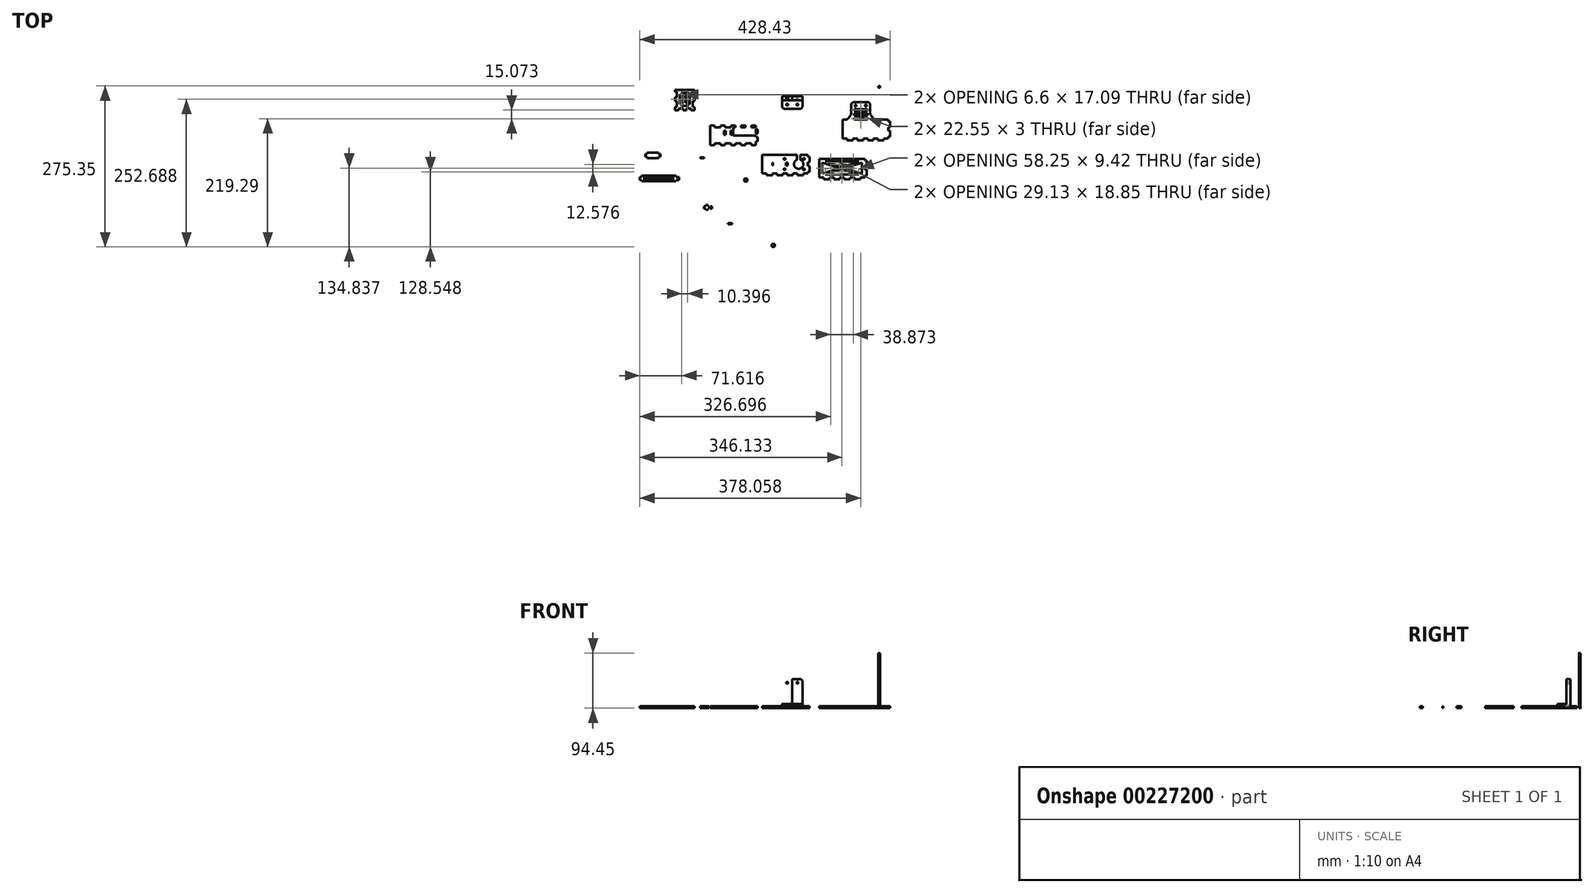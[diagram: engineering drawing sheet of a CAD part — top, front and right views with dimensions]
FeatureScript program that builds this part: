
annotation { "Feature Type Name" : "Feature", "Feature Type Description" : "" }
export const myFeature = defineFeature(function(context is Context, id is Id, definition is map)
    precondition{}
    {
        {
            var Q0;
            Q0=qCreatedBy(makeId("Top.planeOp"),FACE);
            var sketch = newSketch(context, id + "F0", { "sketchPlane" : qUnion([Q0])});
            skLineSegment(sketch, "E0.bottom", {"start": v(-53.14, -63.15) * mm, "end": v(-99.14, -63.15) * mm});
            skLineSegment(sketch, "E0.top", {"start": v(-53.14, -95.15) * mm, "end": v(-99.14, -95.15) * mm});
            skLineSegment(sketch, "E0.left", {"start": v(-53.14, -63.15) * mm, "end": v(-53.14, -95.15) * mm});
            skLineSegment(sketch, "E0.right", {"start": v(-99.14, -63.15) * mm, "end": v(-99.14, -95.15) * mm, "construction": true});
            skPoint(sketch, "E0.middle", {"position": v(-76.14, -79.15) * mm});
            skCircle(sketch, "E1", {"center": v(-58.64, -70.15) * mm, "radius": 1.5 * mm});
            skLineSegment(sketch, "E2.bottom", {"start": v(-141.01, -16.5) * mm, "end": v(-219.01, -16.5) * mm});
            skLineSegment(sketch, "E2.top", {"start": v(-141.01, -43.5) * mm, "end": v(-219.01, -43.5) * mm});
            skLineSegment(sketch, "E2.left", {"start": v(-141.01, -16.5) * mm, "end": v(-141.01, -43.5) * mm});
            skPoint(sketch, "E2.middle", {"position": v(-180.01, -30) * mm});
            skLineSegment(sketch, "E3", {"start": v(-99.14, -63.15) * mm, "end": v(-100.14, -63.15) * mm});
            skLineSegment(sketch, "E4", {"start": v(-100.14, -63.15) * mm, "end": v(-100.14, -95.15) * mm, "construction": true});
            skLineSegment(sketch, "E5", {"start": v(-100.14, -95.15) * mm, "end": v(-99.14, -95.15) * mm});
            skLineSegment(sketch, "E6.MirrorCS", {"start": v(-52.14, -63.15) * mm, "end": v(-52.14, -95.15) * mm});
            skLineSegment(sketch, "E7.MirrorCS", {"start": v(-53.14, -63.15) * mm, "end": v(-52.14, -63.15) * mm});
            skLineSegment(sketch, "E8.MirrorCS", {"start": v(-52.14, -95.15) * mm, "end": v(-53.14, -95.15) * mm});
            skLineSegment(sketch, "E9.MirrorCS", {"start": v(-52.14, -66.15) * mm, "end": v(-48.96, -66.15) * mm});
            skLineSegment(sketch, "E10.MirrorCS", {"start": v(-48.96, -66.15) * mm, "end": v(-48.96, -76.15) * mm});
            skLineSegment(sketch, "E11.MirrorCS", {"start": v(-48.96, -76.15) * mm, "end": v(-52.14, -76.15) * mm});
            skLineSegment(sketch, "E12.MirrorCS", {"start": v(-48.96, -82.15) * mm, "end": v(-52.14, -82.15) * mm});
            skLineSegment(sketch, "E13.MirrorCS", {"start": v(-48.96, -92.15) * mm, "end": v(-48.96, -82.15) * mm});
            skLineSegment(sketch, "E14.MirrorCS", {"start": v(-52.14, -92.15) * mm, "end": v(-48.96, -92.15) * mm});
            skCircle(sketch, "E15", {"center": v(-67.64, -79.15) * mm, "radius": 8 * mm});
            skLineSegment(sketch, "E16.bottom", {"start": v(-141.01, -19.5) * mm, "end": v(-137.84, -19.5) * mm});
            skLineSegment(sketch, "E16.top", {"start": v(-141.01, -27) * mm, "end": v(-137.84, -27) * mm});
            skLineSegment(sketch, "E16.left", {"start": v(-141.01, -19.5) * mm, "end": v(-141.01, -27) * mm});
            skLineSegment(sketch, "E16.right", {"start": v(-137.84, -19.5) * mm, "end": v(-137.84, -27) * mm});
            skLineSegment(sketch, "E17", {"start": v(-100.14, -63.15) * mm, "end": v(-130.14, -63.15) * mm});
            skLineSegment(sketch, "E18", {"start": v(-130.14, -63.15) * mm, "end": v(-130.14, -95.15) * mm});
            skLineSegment(sketch, "E19", {"start": v(-130.14, -95.15) * mm, "end": v(-100.14, -95.15) * mm});
            skLineSegment(sketch, "E20", {"start": v(-122.54, -95.15) * mm, "end": v(-122.54, -98.32) * mm});
            skLineSegment(sketch, "E21", {"start": v(-122.54, -98.32) * mm, "end": v(-112.54, -98.32) * mm});
            skLineSegment(sketch, "E22", {"start": v(-112.54, -98.32) * mm, "end": v(-112.54, -95.15) * mm});
            skLineSegment(sketch, "E23", {"start": v(-104.94, -95.15) * mm, "end": v(-104.94, -98.32) * mm});
            skLineSegment(sketch, "E24", {"start": v(-104.94, -98.32) * mm, "end": v(-94.94, -98.32) * mm});
            skLineSegment(sketch, "E25", {"start": v(-94.94, -98.32) * mm, "end": v(-94.94, -95.15) * mm});
            skLineSegment(sketch, "E26", {"start": v(-87.34, -95.15) * mm, "end": v(-87.34, -98.32) * mm});
            skLineSegment(sketch, "E27", {"start": v(-87.34, -98.32) * mm, "end": v(-77.34, -98.32) * mm});
            skLineSegment(sketch, "E28", {"start": v(-77.34, -98.32) * mm, "end": v(-77.34, -95.15) * mm});
            skLineSegment(sketch, "E29", {"start": v(-69.74, -95.15) * mm, "end": v(-69.74, -98.32) * mm});
            skLineSegment(sketch, "E30", {"start": v(-69.74, -98.32) * mm, "end": v(-59.74, -98.32) * mm});
            skLineSegment(sketch, "E31", {"start": v(-59.74, -98.32) * mm, "end": v(-59.74, -95.15) * mm});
            skLineSegment(sketch, "E32", {"start": v(-219.01, -43.5) * mm, "end": v(-219.01, -46.67) * mm});
            skLineSegment(sketch, "E33", {"start": v(-219.01, -46.67) * mm, "end": v(-211.41, -46.67) * mm});
            skLineSegment(sketch, "E34", {"start": v(-211.41, -46.67) * mm, "end": v(-211.41, -43.5) * mm});
            skLineSegment(sketch, "E35", {"start": v(-201.41, -43.5) * mm, "end": v(-201.41, -46.66) * mm});
            skLineSegment(sketch, "E36", {"start": v(-201.41, -46.66) * mm, "end": v(-193.81, -46.66) * mm});
            skLineSegment(sketch, "E37", {"start": v(-193.81, -46.66) * mm, "end": v(-193.81, -43.48) * mm});
            skLineSegment(sketch, "E38", {"start": v(-183.81, -43.5) * mm, "end": v(-183.81, -46.66) * mm});
            skLineSegment(sketch, "E39", {"start": v(-183.81, -46.66) * mm, "end": v(-176.21, -46.66) * mm});
            skLineSegment(sketch, "E40", {"start": v(-176.21, -46.66) * mm, "end": v(-176.21, -43.5) * mm});
            skLineSegment(sketch, "E41", {"start": v(-166.21, -43.5) * mm, "end": v(-166.21, -46.67) * mm});
            skLineSegment(sketch, "E42", {"start": v(-166.21, -46.67) * mm, "end": v(-158.61, -46.67) * mm});
            skLineSegment(sketch, "E43", {"start": v(-158.61, -46.67) * mm, "end": v(-158.61, -43.5) * mm});
            skLineSegment(sketch, "E44", {"start": v(-148.61, -43.5) * mm, "end": v(-148.61, -46.67) * mm});
            skLineSegment(sketch, "E45", {"start": v(-148.61, -46.67) * mm, "end": v(-141.01, -46.67) * mm});
            skLineSegment(sketch, "E46", {"start": v(-141.01, -46.67) * mm, "end": v(-141.01, -43.5) * mm});
            skLineSegment(sketch, "E47.MirrorCS", {"start": v(45.62, -69.95) * mm, "end": v(45.62, -101.95) * mm});
            skLineSegment(sketch, "E48.MirrorCS", {"start": v(44.62, -68.51) * mm, "end": v(45.62, -68.51) * mm});
            skLineSegment(sketch, "E49.MirrorCS", {"start": v(48.8, -72.95) * mm, "end": v(48.8, -82.95) * mm});
            skLineSegment(sketch, "E50.MirrorCS", {"start": v(48.8, -98.95) * mm, "end": v(48.8, -88.95) * mm});
            skLineSegment(sketch, "E51", {"start": v(-32.38, -69.95) * mm, "end": v(-32.38, -101.95) * mm});
            skLineSegment(sketch, "E52", {"start": v(-24.78, -101.95) * mm, "end": v(-24.78, -105.13) * mm});
            skLineSegment(sketch, "E53", {"start": v(-24.78, -105.13) * mm, "end": v(-14.78, -105.13) * mm});
            skLineSegment(sketch, "E54", {"start": v(-14.78, -105.13) * mm, "end": v(-14.78, -101.95) * mm});
            skLineSegment(sketch, "E55", {"start": v(-7.18, -101.95) * mm, "end": v(-7.18, -105.13) * mm});
            skLineSegment(sketch, "E56", {"start": v(-7.18, -105.13) * mm, "end": v(2.82, -105.13) * mm});
            skLineSegment(sketch, "E57", {"start": v(2.82, -105.13) * mm, "end": v(2.82, -101.95) * mm});
            skLineSegment(sketch, "E58", {"start": v(10.42, -101.95) * mm, "end": v(10.42, -105.13) * mm});
            skLineSegment(sketch, "E59", {"start": v(10.42, -105.13) * mm, "end": v(20.42, -105.13) * mm});
            skLineSegment(sketch, "E60", {"start": v(20.42, -105.13) * mm, "end": v(20.42, -101.95) * mm});
            skLineSegment(sketch, "E61", {"start": v(28.02, -101.95) * mm, "end": v(28.02, -105.13) * mm});
            skLineSegment(sketch, "E62", {"start": v(28.02, -105.13) * mm, "end": v(38.02, -105.13) * mm});
            skLineSegment(sketch, "E63", {"start": v(38.02, -105.13) * mm, "end": v(38.02, -101.95) * mm});
            skLineSegment(sketch, "E64.bottom", {"start": v(-249.2, 47.9) * mm, "end": v(-276.2, 47.9) * mm});
            skLineSegment(sketch, "E64.top", {"start": v(-249.2, 15.9) * mm, "end": v(-276.2, 15.9) * mm});
            skLineSegment(sketch, "E64.left", {"start": v(-249.2, 47.9) * mm, "end": v(-249.2, 15.9) * mm});
            skLineSegment(sketch, "E64.right", {"start": v(-276.2, 47.9) * mm, "end": v(-276.2, 15.9) * mm});
            skPoint(sketch, "E64.middle", {"position": v(-262.7, 31.9) * mm});
            skLineSegment(sketch, "E65", {"start": v(-262.7, 47.9) * mm, "end": v(-262.7, 15.9) * mm, "construction": true});
            skLineSegment(sketch, "E66", {"start": v(-265.7, 15.9) * mm, "end": v(-265.7, 12.72) * mm});
            skLineSegment(sketch, "E67", {"start": v(-265.7, 12.72) * mm, "end": v(-259.7, 12.72) * mm});
            skLineSegment(sketch, "E68", {"start": v(-259.7, 12.72) * mm, "end": v(-259.7, 15.9) * mm});
            skLineSegment(sketch, "E69", {"start": v(-252.2, 12.72) * mm, "end": v(-252.2, 15.9) * mm});
            skLineSegment(sketch, "E70", {"start": v(-249.2, 34.9) * mm, "end": v(-245.88, 34.9) * mm});
            skLineSegment(sketch, "E71", {"start": v(-245.88, 34.9) * mm, "end": v(-245.88, 28.9) * mm});
            skLineSegment(sketch, "E72", {"start": v(-245.88, 28.9) * mm, "end": v(-249.2, 28.9) * mm});
            skLineSegment(sketch, "E73", {"start": v(-249.2, 47.9) * mm, "end": v(-245.88, 47.9) * mm});
            skLineSegment(sketch, "E74", {"start": v(-245.88, 47.9) * mm, "end": v(-245.88, 44.9) * mm});
            skLineSegment(sketch, "E75", {"start": v(-245.88, 44.9) * mm, "end": v(-249.2, 44.9) * mm});
            skLineSegment(sketch, "E76", {"start": v(-276.2, 31.9) * mm, "end": v(-249.2, 31.9) * mm, "construction": true});
            skLineSegment(sketch, "E77.MirrorCS", {"start": v(-245.88, 18.9) * mm, "end": v(-249.2, 18.9) * mm});
            skLineSegment(sketch, "E78.MirrorCS", {"start": v(-245.88, 15.9) * mm, "end": v(-245.88, 18.9) * mm});
            skLineSegment(sketch, "E79.MirrorCS", {"start": v(-249.2, 15.9) * mm, "end": v(-245.88, 15.9) * mm});
            skLineSegment(sketch, "E80.MirrorCS", {"start": v(-276.2, 47.9) * mm, "end": v(-279.5, 47.9) * mm});
            skLineSegment(sketch, "E81.MirrorCS", {"start": v(-279.5, 44.9) * mm, "end": v(-276.2, 44.9) * mm});
            skLineSegment(sketch, "E82.MirrorCS", {"start": v(-279.5, 47.9) * mm, "end": v(-279.5, 44.9) * mm});
            skLineSegment(sketch, "E83.MirrorCS", {"start": v(-276.2, 34.9) * mm, "end": v(-279.5, 34.9) * mm});
            skLineSegment(sketch, "E84.MirrorCS", {"start": v(-279.5, 34.9) * mm, "end": v(-279.5, 28.9) * mm});
            skLineSegment(sketch, "E85.MirrorCS", {"start": v(-279.5, 28.9) * mm, "end": v(-276.2, 28.9) * mm});
            skLineSegment(sketch, "E86.MirrorCS", {"start": v(-279.5, 18.9) * mm, "end": v(-276.2, 18.9) * mm});
            skLineSegment(sketch, "E87.MirrorCS", {"start": v(-276.2, 15.9) * mm, "end": v(-279.5, 15.9) * mm});
            skLineSegment(sketch, "E88.MirrorCS", {"start": v(-279.5, 15.9) * mm, "end": v(-279.5, 18.9) * mm});
            skLineSegment(sketch, "E89", {"start": v(-252.2, 12.72) * mm, "end": v(-245.88, 12.72) * mm});
            skLineSegment(sketch, "E90", {"start": v(-245.88, 12.72) * mm, "end": v(-245.88, 15.9) * mm});
            skLineSegment(sketch, "E91.MirrorCS", {"start": v(-273.2, 12.72) * mm, "end": v(-273.2, 15.9) * mm});
            skLineSegment(sketch, "E92.MirrorCS", {"start": v(-273.2, 12.72) * mm, "end": v(-279.5, 12.72) * mm});
            skLineSegment(sketch, "E93.MirrorCS", {"start": v(-279.5, 12.72) * mm, "end": v(-279.5, 15.9) * mm});
            skLineSegment(sketch, "E94.bottom", {"start": v(-254.2, 42.9) * mm, "end": v(-271.2, 42.9) * mm});
            skLineSegment(sketch, "E94.top", {"start": v(-254.2, 20.9) * mm, "end": v(-271.2, 20.9) * mm});
            skLineSegment(sketch, "E94.left", {"start": v(-254.2, 42.9) * mm, "end": v(-254.2, 20.9) * mm});
            skLineSegment(sketch, "E94.right", {"start": v(-271.2, 42.9) * mm, "end": v(-271.2, 20.9) * mm});
            skLineSegment(sketch, "E95", {"start": v(-271.2, 42.9) * mm, "end": v(-254.2, 20.9) * mm, "construction": true});
            skLineSegment(sketch, "E96", {"start": v(-269.3, 42.9) * mm, "end": v(-254.2, 23.35) * mm});
            skLineSegment(sketch, "E97", {"start": v(-271.2, 40.44) * mm, "end": v(-256.1, 20.9) * mm});
            skLineSegment(sketch, "E98", {"start": v(-271.2, 20.9) * mm, "end": v(-254.2, 42.9) * mm, "construction": true});
            skLineSegment(sketch, "E99", {"start": v(-271.2, 23.35) * mm, "end": v(-256.1, 42.9) * mm});
            skLineSegment(sketch, "E100", {"start": v(-269.3, 20.9) * mm, "end": v(-254.2, 40.44) * mm});
            skLineSegment(sketch, "E101", {"start": v(-32.38, -85.95) * mm, "end": v(45.62, -85.95) * mm, "construction": true});
            skLineSegment(sketch, "E102.bottom", {"start": v(40.62, -74.95) * mm, "end": v(-27.38, -74.95) * mm});
            skLineSegment(sketch, "E102.top", {"start": v(40.62, -96.95) * mm, "end": v(-27.38, -96.95) * mm});
            skLineSegment(sketch, "E102.left", {"start": v(40.62, -74.95) * mm, "end": v(40.62, -96.95) * mm});
            skLineSegment(sketch, "E102.right", {"start": v(-27.38, -74.95) * mm, "end": v(-27.38, -96.95) * mm});
            skPoint(sketch, "E102.middle", {"position": v(6.62, -85.95) * mm});
            skLineSegment(sketch, "E103", {"start": v(-32.38, -69.95) * mm, "end": v(45.62, -69.95) * mm});
            skLineSegment(sketch, "E104", {"start": v(-32.38, -101.95) * mm, "end": v(45.62, -101.95) * mm});
            skLineSegment(sketch, "E105", {"start": v(48.8, -72.95) * mm, "end": v(45.62, -72.95) * mm});
            skLineSegment(sketch, "E106", {"start": v(48.8, -82.95) * mm, "end": v(45.62, -82.95) * mm});
            skLineSegment(sketch, "E107", {"start": v(48.8, -88.95) * mm, "end": v(45.62, -88.95) * mm});
            skLineSegment(sketch, "E108", {"start": v(48.8, -98.95) * mm, "end": v(45.62, -98.95) * mm});
            skLineSegment(sketch, "E109", {"start": v(-27.38, -74.95) * mm, "end": v(40.62, -96.95) * mm, "construction": true});
            skLineSegment(sketch, "E110", {"start": v(40.62, -74.95) * mm, "end": v(-27.38, -96.95) * mm, "construction": true});
            skLineSegment(sketch, "E111", {"start": v(-27.38, -76.53) * mm, "end": v(35.75, -96.95) * mm});
            skLineSegment(sketch, "E112", {"start": v(-22.5, -74.95) * mm, "end": v(40.62, -95.38) * mm});
            skLineSegment(sketch, "E113", {"start": v(-27.38, -95.38) * mm, "end": v(35.75, -74.95) * mm});
            skLineSegment(sketch, "E114", {"start": v(-22.5, -96.95) * mm, "end": v(40.62, -76.53) * mm});
            skCircle(sketch, "E115", {"center": v(-58.64, -70.15) * mm, "radius": 4 * mm, "construction": true});
            skCircle(sketch, "E116", {"center": v(-58.64, -88.05) * mm, "radius": 1.5 * mm});
            skCircle(sketch, "E117", {"center": v(-58.64, -88.05) * mm, "radius": 4 * mm, "construction": true});
            skLineSegment(sketch, "E118", {"start": v(-58.64, -66.15) * mm, "end": v(-58.64, -92.05) * mm, "construction": true});
            skCircle(sketch, "E119", {"center": v(-91.74, -70.15) * mm, "radius": 1.5 * mm});
            skCircle(sketch, "E120", {"center": v(-91.74, -70.15) * mm, "radius": 4 * mm, "construction": true});
            skLineSegment(sketch, "E121", {"start": v(-54.64, -70.15) * mm, "end": v(-95.74, -70.15) * mm, "construction": true});
            skCircle(sketch, "E122", {"center": v(-91.74, -88.05) * mm, "radius": 4 * mm, "construction": true});
            skCircle(sketch, "E123", {"center": v(-91.74, -88.05) * mm, "radius": 1.5 * mm});
            skLineSegment(sketch, "E124", {"start": v(-91.74, -66.15) * mm, "end": v(-91.74, -92.05) * mm, "construction": true});
            skLineSegment(sketch, "E125", {"start": v(-95.74, -88.05) * mm, "end": v(-54.64, -88.05) * mm, "construction": true});
            skCircle(sketch, "E126", {"center": v(-67.64, -79.15) * mm, "radius": 3 * mm});
            skLineSegment(sketch, "E127", {"start": v(-64.64, -79.15) * mm, "end": v(-64.64, -63.15) * mm});
            skLineSegment(sketch, "E128", {"start": v(-70.64, -79.15) * mm, "end": v(-70.64, -63.15) * mm});
            skLineSegment(sketch, "E129.bottom", {"start": v(-61.08, 30.24) * mm, "end": v(-96.08, 30.24) * mm});
            skLineSegment(sketch, "E129.top", {"start": v(-61.08, 15.24) * mm, "end": v(-96.08, 15.24) * mm});
            skLineSegment(sketch, "E129.left", {"start": v(-61.08, 30.24) * mm, "end": v(-61.08, 15.24) * mm});
            skLineSegment(sketch, "E129.right", {"start": v(-96.08, 30.24) * mm, "end": v(-96.08, 15.24) * mm});
            skPoint(sketch, "E129.middle", {"position": v(-78.58, 22.74) * mm});
            skLineSegment(sketch, "E130", {"start": v(-78.58, 30.24) * mm, "end": v(-78.58, 15.24) * mm});
            skCircle(sketch, "E131", {"center": v(-69.83, 22.74) * mm, "radius": 1.5 * mm});
            skCircle(sketch, "E132.MirrorC", {"center": v(-87.33, 22.74) * mm, "radius": 1.5 * mm});
            skLineSegment(sketch, "E133.right", {"start": v(-184.3, -29.24) * mm, "end": v(-184.3, -22.24) * mm});
            skPoint(sketch, "E133.middle", {"position": v(-199.51, -30) * mm});
            skLineSegment(sketch, "E134", {"start": v(-180.01, -30) * mm, "end": v(-219.01, -30) * mm});
            skLineSegment(sketch, "E135", {"start": v(-180.01, -30) * mm, "end": v(-141.01, -30) * mm});
            skLineSegment(sketch, "E136", {"start": v(-184.3, -29.24) * mm, "end": v(-181.13, -29.24) * mm});
            skLineSegment(sketch, "E137", {"start": v(-181.13, -29.24) * mm, "end": v(-181.13, -22.24) * mm});
            skLineSegment(sketch, "E138", {"start": v(-181.13, -22.24) * mm, "end": v(-184.3, -22.24) * mm});
            skLineSegment(sketch, "E139.MirrorCS", {"start": v(85.74, -3) * mm, "end": v(85.74, -35) * mm});
            skLineSegment(sketch, "E140.MirrorCS", {"start": v(89.63, 2.18) * mm, "end": v(90.63, 2.18) * mm});
            skLineSegment(sketch, "E141.MirrorCS", {"start": v(88.92, -6) * mm, "end": v(88.92, -16) * mm});
            skLineSegment(sketch, "E142.MirrorCS", {"start": v(88.92, -32) * mm, "end": v(88.92, -22) * mm});
            skLineSegment(sketch, "E143", {"start": v(7.74, -3) * mm, "end": v(7.74, -35) * mm});
            skLineSegment(sketch, "E144", {"start": v(15.34, -35) * mm, "end": v(15.34, -38.17) * mm});
            skLineSegment(sketch, "E145", {"start": v(15.34, -38.17) * mm, "end": v(25.34, -38.17) * mm});
            skLineSegment(sketch, "E146", {"start": v(25.34, -38.17) * mm, "end": v(25.34, -35) * mm});
            skLineSegment(sketch, "E147", {"start": v(32.94, -35) * mm, "end": v(32.94, -38.17) * mm});
            skLineSegment(sketch, "E148", {"start": v(32.94, -38.17) * mm, "end": v(42.94, -38.17) * mm});
            skLineSegment(sketch, "E149", {"start": v(42.94, -38.17) * mm, "end": v(42.94, -35) * mm});
            skLineSegment(sketch, "E150", {"start": v(50.54, -35) * mm, "end": v(50.54, -38.17) * mm});
            skLineSegment(sketch, "E151", {"start": v(50.54, -38.17) * mm, "end": v(60.54, -38.17) * mm});
            skLineSegment(sketch, "E152", {"start": v(60.54, -38.17) * mm, "end": v(60.54, -35) * mm});
            skLineSegment(sketch, "E153", {"start": v(68.14, -35) * mm, "end": v(68.14, -38.17) * mm});
            skLineSegment(sketch, "E154", {"start": v(68.14, -38.17) * mm, "end": v(78.14, -38.17) * mm});
            skLineSegment(sketch, "E155", {"start": v(78.14, -38.17) * mm, "end": v(78.14, -35) * mm});
            skPoint(sketch, "E156.middle", {"position": v(51.63, -13.82) * mm});
            skLineSegment(sketch, "E157", {"start": v(7.74, -3) * mm, "end": v(85.74, -3) * mm});
            skLineSegment(sketch, "E158", {"start": v(7.74, -35) * mm, "end": v(85.74, -35) * mm});
            skLineSegment(sketch, "E159", {"start": v(88.92, -6) * mm, "end": v(85.74, -6) * mm});
            skLineSegment(sketch, "E160", {"start": v(88.92, -16) * mm, "end": v(85.74, -16) * mm});
            skLineSegment(sketch, "E161", {"start": v(88.92, -22) * mm, "end": v(85.74, -22) * mm});
            skLineSegment(sketch, "E162", {"start": v(88.92, -32) * mm, "end": v(85.74, -32) * mm});
            skLineSegment(sketch, "E163.bottom", {"start": v(7.74, -35) * mm, "end": v(-10.26, -35) * mm});
            skLineSegment(sketch, "E163.top", {"start": v(7.74, -3) * mm, "end": v(-10.26, -3) * mm});
            skLineSegment(sketch, "E163.left", {"start": v(7.74, -35) * mm, "end": v(7.74, -3) * mm});
            skLineSegment(sketch, "E163.right", {"start": v(-10.26, -35) * mm, "end": v(-10.26, -3) * mm});
            skCircle(sketch, "E164", {"center": v(70.28, 53.06) * mm, "radius": 1.5 * mm});
            skLineSegment(sketch, "E165", {"start": v(-10.26, -25.65) * mm, "end": v(7.74, -25.65) * mm});
            skLineSegment(sketch, "E166", {"start": v(-10.26, -21.6) * mm, "end": v(7.74, -21.6) * mm});
            skLineSegment(sketch, "E167", {"start": v(7.74, -35) * mm, "end": v(-10.26, -21.6) * mm});
            skLineSegment(sketch, "E168", {"start": v(-160.5, -101.33) * mm, "end": v(-226.37, -69.2) * mm});
            skLineSegment(sketch, "E169", {"start": v(-226.37, -69.2) * mm, "end": v(-252.35, -69.2) * mm});
            skLineSegment(sketch, "E170", {"start": v(-160.5, -114) * mm, "end": v(-160.5, -101.33) * mm});
            skLineSegment(sketch, "E171", {"start": v(-252.35, -69.2) * mm, "end": v(-160.5, -114) * mm});
            skLineSegment(sketch, "E172", {"start": v(-160.5, -114) * mm, "end": v(-160.5, -69.2) * mm});
            skLineSegment(sketch, "E173", {"start": v(-160.5, -69.2) * mm, "end": v(-252.35, -69.2) * mm, "construction": true});
            skLineSegment(sketch, "E174.bottom", {"start": v(-160.5, -104.01) * mm, "end": v(-155.42, -104.01) * mm});
            skLineSegment(sketch, "E174.top", {"start": v(-160.5, -109.01) * mm, "end": v(-155.42, -109.01) * mm});
            skLineSegment(sketch, "E174.left", {"start": v(-160.5, -104.01) * mm, "end": v(-160.5, -109.01) * mm});
            skLineSegment(sketch, "E174.right", {"start": v(-155.42, -104.01) * mm, "end": v(-155.42, -109.01) * mm});
            skLineSegment(sketch, "E175", {"start": v(-249.28, -70.7) * mm, "end": v(-160.5, -70.7) * mm});
            skLineSegment(sketch, "E176", {"start": v(-160.5, -110.49) * mm, "end": v(-167.7, -110.49) * mm});
            skLineSegment(sketch, "E177", {"start": v(-160.5, -110.49) * mm, "end": v(-242.08, -70.7) * mm});
            skLineSegment(sketch, "E178.bottom", {"start": v(-236.19, -70.7) * mm, "end": v(-229.19, -70.7) * mm});
            skLineSegment(sketch, "E178.top", {"start": v(-236.19, -67.53) * mm, "end": v(-229.19, -67.53) * mm});
            skLineSegment(sketch, "E178.left", {"start": v(-236.19, -70.7) * mm, "end": v(-236.19, -67.53) * mm});
            skLineSegment(sketch, "E178.right", {"start": v(-229.19, -70.7) * mm, "end": v(-229.19, -67.53) * mm});
            skLineSegment(sketch, "E179", {"start": v(-87.33, 22.74) * mm, "end": v(-69.83, 22.74) * mm});
            skLineSegment(sketch, "E180.bottom", {"start": v(-192.13, -29.24) * mm, "end": v(-195.3, -29.24) * mm});
            skLineSegment(sketch, "E180.top", {"start": v(-192.13, -22.24) * mm, "end": v(-195.3, -22.24) * mm});
            skLineSegment(sketch, "E180.left", {"start": v(-192.13, -29.24) * mm, "end": v(-192.13, -22.24) * mm});
            skLineSegment(sketch, "E180.right", {"start": v(-195.3, -29.24) * mm, "end": v(-195.3, -22.24) * mm});
            skLineSegment(sketch, "E181", {"start": v(-193.71, -29.24) * mm, "end": v(-193.71, -22.24) * mm});
            skLineSegment(sketch, "E182", {"start": v(-182.71, -29.24) * mm, "end": v(-182.71, -22.24) * mm});
            skLineSegment(sketch, "E183", {"start": v(-219.01, -43.5) * mm, "end": v(-219.01, -16.5) * mm});
            skLineSegment(sketch, "E184", {"start": v(-180.01, -46.66) * mm, "end": v(-180.01, -9.6) * mm});
            skLineSegment(sketch, "E185.MirrorCS", {"start": v(-219.01, -13.32) * mm, "end": v(-211.41, -13.32) * mm});
            skLineSegment(sketch, "E186.MirrorCS", {"start": v(-219.01, -16.5) * mm, "end": v(-219.01, -13.32) * mm});
            skLineSegment(sketch, "E187.MirrorCS", {"start": v(-211.41, -13.32) * mm, "end": v(-211.41, -16.5) * mm});
            skLineSegment(sketch, "E188.MirrorCS", {"start": v(-201.41, -13.34) * mm, "end": v(-193.81, -13.34) * mm});
            skLineSegment(sketch, "E189.MirrorCS", {"start": v(-201.41, -16.5) * mm, "end": v(-201.41, -13.34) * mm});
            skLineSegment(sketch, "E190.MirrorCS", {"start": v(-193.81, -13.34) * mm, "end": v(-193.81, -16.51) * mm});
            skLineSegment(sketch, "E191.MirrorCS", {"start": v(-183.81, -13.34) * mm, "end": v(-176.21, -13.34) * mm});
            skLineSegment(sketch, "E192.MirrorCS", {"start": v(-183.81, -16.5) * mm, "end": v(-183.81, -13.34) * mm});
            skLineSegment(sketch, "E193.MirrorCS", {"start": v(-176.21, -13.34) * mm, "end": v(-176.21, -16.5) * mm});
            skLineSegment(sketch, "E194.MirrorCS", {"start": v(-166.21, -13.32) * mm, "end": v(-158.61, -13.32) * mm});
            skLineSegment(sketch, "E195.MirrorCS", {"start": v(-166.21, -16.5) * mm, "end": v(-166.21, -13.32) * mm});
            skLineSegment(sketch, "E196.MirrorCS", {"start": v(-158.61, -13.32) * mm, "end": v(-158.61, -16.5) * mm});
            skLineSegment(sketch, "E197.MirrorCS", {"start": v(-148.61, -16.5) * mm, "end": v(-148.61, -13.32) * mm});
            skLineSegment(sketch, "E198.MirrorCS", {"start": v(-148.61, -13.32) * mm, "end": v(-141.01, -13.32) * mm});
            skLineSegment(sketch, "E199.MirrorCS", {"start": v(-141.01, -13.32) * mm, "end": v(-141.01, -16.5) * mm});
            skLineSegment(sketch, "E200.MirrorCS", {"start": v(-141.01, -33) * mm, "end": v(-137.84, -33) * mm});
            skLineSegment(sketch, "E201.MirrorCS", {"start": v(-137.84, -40.5) * mm, "end": v(-137.84, -33) * mm});
            skLineSegment(sketch, "E202.MirrorCS", {"start": v(-141.01, -40.5) * mm, "end": v(-137.84, -40.5) * mm});
            skLineSegment(sketch, "E203.bottom", {"start": v(-108.6, -81.58) * mm, "end": v(-111.78, -81.58) * mm});
            skLineSegment(sketch, "E203.top", {"start": v(-108.6, -76.58) * mm, "end": v(-111.78, -76.58) * mm});
            skLineSegment(sketch, "E203.left", {"start": v(-108.6, -81.58) * mm, "end": v(-108.6, -76.58) * mm});
            skLineSegment(sketch, "E204", {"start": v(-111.78, -81.58) * mm, "end": v(-111.78, -76.58) * mm});
            skLineSegment(sketch, "E205.bottom", {"start": v(-121.6, 103.53) * mm, "end": v(-39.32, 103.53) * mm});
            skLineSegment(sketch, "E205.top", {"start": v(-121.6, 92.37) * mm, "end": v(-39.32, 92.37) * mm});
            skLineSegment(sketch, "E205.left", {"start": v(-121.6, 103.53) * mm, "end": v(-121.6, 92.37) * mm});
            skLineSegment(sketch, "E205.right", {"start": v(-39.32, 103.53) * mm, "end": v(-39.32, 92.37) * mm});
            skPoint(sketch, "E205.middle", {"position": v(-80.46, 97.95) * mm});
            skLineSegment(sketch, "E206", {"start": v(-80.46, 103.53) * mm, "end": v(-80.46, 92.37) * mm});
            skLineSegment(sketch, "E207", {"start": v(-113.85, -213.56) * mm, "end": v(-178.5, -182.02) * mm});
            skLineSegment(sketch, "E208", {"start": v(-178.5, -182.02) * mm, "end": v(-204.48, -182.02) * mm});
            skLineSegment(sketch, "E209", {"start": v(-113.85, -226.23) * mm, "end": v(-113.85, -213.56) * mm});
            skLineSegment(sketch, "E210", {"start": v(-204.48, -182.02) * mm, "end": v(-113.85, -226.23) * mm});
            skLineSegment(sketch, "E211", {"start": v(-113.85, -226.23) * mm, "end": v(-113.85, -182.02) * mm});
            skLineSegment(sketch, "E212", {"start": v(-113.85, -182.02) * mm, "end": v(-204.48, -182.02) * mm, "construction": true});
            skLineSegment(sketch, "E213.bottom", {"start": v(-113.85, -215.79) * mm, "end": v(-108.77, -215.79) * mm});
            skLineSegment(sketch, "E213.top", {"start": v(-113.85, -220.79) * mm, "end": v(-108.77, -220.79) * mm});
            skLineSegment(sketch, "E213.left", {"start": v(-113.85, -215.79) * mm, "end": v(-113.85, -220.79) * mm});
            skLineSegment(sketch, "E213.right", {"start": v(-108.77, -215.79) * mm, "end": v(-108.77, -220.79) * mm});
            skLineSegment(sketch, "E214", {"start": v(-201.41, -183.52) * mm, "end": v(-113.85, -183.52) * mm});
            skLineSegment(sketch, "E215", {"start": v(-113.85, -222.72) * mm, "end": v(-121.05, -222.72) * mm});
            skLineSegment(sketch, "E216", {"start": v(-113.85, -222.72) * mm, "end": v(-194.21, -183.52) * mm});
            skLineSegment(sketch, "E217.bottom", {"start": v(-188.33, -183.52) * mm, "end": v(-181.33, -183.52) * mm});
            skLineSegment(sketch, "E217.top", {"start": v(-188.33, -180.34) * mm, "end": v(-181.33, -180.34) * mm});
            skLineSegment(sketch, "E217.left", {"start": v(-188.33, -183.52) * mm, "end": v(-188.33, -180.34) * mm});
            skLineSegment(sketch, "E217.right", {"start": v(-181.33, -183.52) * mm, "end": v(-181.33, -180.34) * mm});
            skLineSegment(sketch, "E218.bottom", {"start": v(-219.33, -149.2) * mm, "end": v(-226.94, -149.2) * mm});
            skLineSegment(sketch, "E218.top", {"start": v(-219.33, -157.42) * mm, "end": v(-226.94, -157.42) * mm});
            skLineSegment(sketch, "E218.left", {"start": v(-219.33, -149.2) * mm, "end": v(-219.33, -157.42) * mm});
            skLineSegment(sketch, "E218.right", {"start": v(-226.94, -149.2) * mm, "end": v(-226.94, -157.42) * mm});
            skPoint(sketch, "E218.middle", {"position": v(-223.13, -153.3) * mm});
            skLineSegment(sketch, "E219.bottom", {"start": v(-219.33, -151.3) * mm, "end": v(-216.15, -151.3) * mm});
            skLineSegment(sketch, "E219.top", {"start": v(-219.33, -155.3) * mm, "end": v(-216.15, -155.3) * mm});
            skLineSegment(sketch, "E219.left", {"start": v(-219.33, -151.3) * mm, "end": v(-219.33, -155.3) * mm});
            skLineSegment(sketch, "E219.right", {"start": v(-216.15, -151.3) * mm, "end": v(-216.15, -155.3) * mm});
            skLineSegment(sketch, "E220", {"start": v(-223.13, -149.2) * mm, "end": v(-223.13, -157.42) * mm});
            skLineSegment(sketch, "E221.MirrorCS", {"start": v(-226.94, -151.3) * mm, "end": v(-230.12, -151.3) * mm});
            skLineSegment(sketch, "E222.MirrorCS", {"start": v(-230.12, -151.3) * mm, "end": v(-230.12, -155.3) * mm});
            skLineSegment(sketch, "E223.MirrorCS", {"start": v(-226.94, -155.3) * mm, "end": v(-230.12, -155.3) * mm});
            skLineSegment(sketch, "E224.bottom", {"start": v(-221.13, -151.3) * mm, "end": v(-225.13, -151.3) * mm});
            skLineSegment(sketch, "E224.top", {"start": v(-221.13, -155.3) * mm, "end": v(-225.13, -155.3) * mm});
            skLineSegment(sketch, "E224.left", {"start": v(-221.13, -151.3) * mm, "end": v(-221.13, -155.3) * mm});
            skLineSegment(sketch, "E224.right", {"start": v(-225.13, -151.3) * mm, "end": v(-225.13, -155.3) * mm});
            skLineSegment(sketch, "E225", {"start": v(-225.13, -151.3) * mm, "end": v(-221.13, -155.3) * mm});
            skLineSegment(sketch, "E226", {"start": v(-221.13, -151.3) * mm, "end": v(-225.13, -155.3) * mm});
            skLineSegment(sketch, "E227", {"start": v(-225.13, -152.01) * mm, "end": v(-221.84, -155.3) * mm});
            skLineSegment(sketch, "E228", {"start": v(-224.43, -151.3) * mm, "end": v(-221.13, -154.6) * mm});
            skLineSegment(sketch, "E229", {"start": v(-225.13, -154.6) * mm, "end": v(-221.84, -151.3) * mm});
            skLineSegment(sketch, "E230", {"start": v(-224.43, -155.3) * mm, "end": v(-221.13, -152.01) * mm});
            skLineSegment(sketch, "E231.bottom", {"start": v(-100.57, -76.58) * mm, "end": v(-97.4, -76.58) * mm});
            skLineSegment(sketch, "E231.top", {"start": v(-100.57, -81.58) * mm, "end": v(-97.4, -81.58) * mm});
            skLineSegment(sketch, "E231.left", {"start": v(-100.57, -76.58) * mm, "end": v(-100.57, -81.58) * mm});
            skLineSegment(sketch, "E231.right", {"start": v(-97.4, -76.58) * mm, "end": v(-97.4, -81.58) * mm});
            skLineSegment(sketch, "E232.bottom", {"start": v(-89.36, -76.58) * mm, "end": v(-86.18, -76.58) * mm});
            skLineSegment(sketch, "E232.top", {"start": v(-89.36, -81.58) * mm, "end": v(-86.18, -81.58) * mm});
            skLineSegment(sketch, "E232.left", {"start": v(-89.36, -76.58) * mm, "end": v(-89.36, -81.58) * mm});
            skLineSegment(sketch, "E232.right", {"start": v(-86.18, -76.58) * mm, "end": v(-86.18, -81.58) * mm});
            skLineSegment(sketch, "E233.bottom", {"start": v(54.82, 27.07) * mm, "end": v(22.27, 27.07) * mm});
            skLineSegment(sketch, "E233.top", {"start": v(54.82, 15.07) * mm, "end": v(22.27, 15.07) * mm});
            skLineSegment(sketch, "E233.left", {"start": v(54.82, 27.07) * mm, "end": v(54.82, 15.07) * mm});
            skLineSegment(sketch, "E233.right", {"start": v(22.27, 27.07) * mm, "end": v(22.27, 15.07) * mm});
            skPoint(sketch, "E233.middle", {"position": v(38.55, 21.07) * mm});
            skLineSegment(sketch, "E234", {"start": v(38.55, 15.07) * mm, "end": v(38.55, -3) * mm, "construction": true});
            skLineSegment(sketch, "E235", {"start": v(34.55, -3) * mm, "end": v(34.55, 15.07) * mm, "construction": true});
            skLineSegment(sketch, "E236.MirrorCS", {"start": v(42.55, -3) * mm, "end": v(42.55, 15.07) * mm, "construction": true});
            skCircle(sketch, "E237", {"center": v(47.3, 21.07) * mm, "radius": 1.5 * mm});
            skLineSegment(sketch, "E238", {"start": v(38.55, 21.07) * mm, "end": v(47.3, 21.07) * mm});
            skCircle(sketch, "E239.MirrorC", {"center": v(29.8, 21.07) * mm, "radius": 1.5 * mm});
            skLineSegment(sketch, "E240.MirrorCS", {"start": v(38.55, 21.07) * mm, "end": v(29.8, 21.07) * mm});
            skLineSegment(sketch, "E241", {"start": v(22.27, 15.07) * mm, "end": v(22.27, -3) * mm});
            skLineSegment(sketch, "E242", {"start": v(54.82, 15.07) * mm, "end": v(54.82, -3) * mm});
            skLineSegment(sketch, "E243", {"start": v(27.27, 15.07) * mm, "end": v(27.27, -3) * mm});
            skLineSegment(sketch, "E244.MirrorCS", {"start": v(49.82, 15.07) * mm, "end": v(49.82, -3) * mm});
            skLineSegment(sketch, "E245", {"start": v(27.27, 12.07) * mm, "end": v(49.82, 12.07) * mm});
            skLineSegment(sketch, "E246", {"start": v(27.27, 8.07) * mm, "end": v(49.82, 8.07) * mm});
            skLineSegment(sketch, "E247", {"start": v(27.27, 4) * mm, "end": v(49.82, 4) * mm});
            skLineSegment(sketch, "E248", {"start": v(27.27, 0) * mm, "end": v(49.82, 0) * mm});
            skLineSegment(sketch, "E249.bottom", {"start": v(-277.77, -99.12) * mm, "end": v(-336.33, -99.12) * mm});
            skLineSegment(sketch, "E249.top", {"start": v(-277.77, -108.12) * mm, "end": v(-336.33, -108.12) * mm});
            skLineSegment(sketch, "E249.left", {"start": v(-277.77, -99.12) * mm, "end": v(-277.77, -108.12) * mm});
            skLineSegment(sketch, "E249.right", {"start": v(-336.33, -99.12) * mm, "end": v(-336.33, -108.12) * mm});
            skPoint(sketch, "E249.middle", {"position": v(-307.05, -103.62) * mm});
            skLineSegment(sketch, "E250.bottom", {"start": v(-277.77, -101.12) * mm, "end": v(-272.7, -101.12) * mm});
            skLineSegment(sketch, "E250.top", {"start": v(-277.77, -106.12) * mm, "end": v(-272.7, -106.12) * mm});
            skLineSegment(sketch, "E250.left", {"start": v(-277.77, -101.12) * mm, "end": v(-277.77, -106.12) * mm});
            skLineSegment(sketch, "E250.right", {"start": v(-272.7, -101.12) * mm, "end": v(-272.7, -106.12) * mm});
            skLineSegment(sketch, "E251.bottom", {"start": v(-336.33, -101.12) * mm, "end": v(-339.5, -101.12) * mm});
            skLineSegment(sketch, "E251.top", {"start": v(-336.33, -106.12) * mm, "end": v(-339.5, -106.12) * mm});
            skLineSegment(sketch, "E251.left", {"start": v(-336.33, -101.12) * mm, "end": v(-336.33, -106.12) * mm});
            skLineSegment(sketch, "E251.right", {"start": v(-339.5, -101.12) * mm, "end": v(-339.5, -106.12) * mm});
            skPoint(sketch, "E252.oppositeSnap0", {"position": v(-110.2, -76.58) * mm});
            skLineSegment(sketch, "E252.bottom", {"start": v(-109.36, -81.58) * mm, "end": v(-112.53, -81.58) * mm});
            skLineSegment(sketch, "E252.top", {"start": v(-109.36, -76.58) * mm, "end": v(-112.53, -76.58) * mm});
            skLineSegment(sketch, "E252.left", {"start": v(-109.36, -81.58) * mm, "end": v(-109.36, -76.58) * mm});
            skLineSegment(sketch, "E252.right", {"start": v(-112.53, -81.58) * mm, "end": v(-112.53, -76.58) * mm});
            skLineSegment(sketch, "E253", {"start": v(-336.33, -103.62) * mm, "end": v(-277.77, -103.62) * mm});
            skLineSegment(sketch, "E254.bottom", {"start": v(-328.61, -101.12) * mm, "end": v(-331.79, -101.12) * mm});
            skLineSegment(sketch, "E254.top", {"start": v(-328.61, -106.12) * mm, "end": v(-331.79, -106.12) * mm});
            skLineSegment(sketch, "E254.left", {"start": v(-328.61, -101.12) * mm, "end": v(-328.61, -106.12) * mm});
            skLineSegment(sketch, "E254.right", {"start": v(-331.79, -101.12) * mm, "end": v(-331.79, -106.12) * mm});
            skPoint(sketch, "E254.middle", {"position": v(-330.2, -103.62) * mm});
            skLineSegment(sketch, "E255.bottom", {"start": v(-320.9, -101.12) * mm, "end": v(-324.07, -101.12) * mm});
            skLineSegment(sketch, "E255.top", {"start": v(-320.9, -106.12) * mm, "end": v(-324.07, -106.12) * mm});
            skLineSegment(sketch, "E255.left", {"start": v(-320.9, -101.12) * mm, "end": v(-320.9, -106.12) * mm});
            skLineSegment(sketch, "E255.right", {"start": v(-324.07, -101.12) * mm, "end": v(-324.07, -106.12) * mm});
            skPoint(sketch, "E255.middle", {"position": v(-322.48, -103.62) * mm});
            skLineSegment(sketch, "E256.bottom", {"start": v(-313.18, -101.12) * mm, "end": v(-316.35, -101.12) * mm});
            skLineSegment(sketch, "E256.top", {"start": v(-313.18, -106.12) * mm, "end": v(-316.35, -106.12) * mm});
            skLineSegment(sketch, "E256.left", {"start": v(-313.18, -101.12) * mm, "end": v(-313.18, -106.12) * mm});
            skLineSegment(sketch, "E256.right", {"start": v(-316.35, -101.12) * mm, "end": v(-316.35, -106.12) * mm});
            skPoint(sketch, "E256.middle", {"position": v(-314.77, -103.62) * mm});
            skLineSegment(sketch, "E257.bottom", {"start": v(-305.46, -101.12) * mm, "end": v(-308.64, -101.12) * mm});
            skLineSegment(sketch, "E257.top", {"start": v(-305.46, -106.12) * mm, "end": v(-308.64, -106.12) * mm});
            skLineSegment(sketch, "E257.left", {"start": v(-305.46, -101.12) * mm, "end": v(-305.46, -106.12) * mm});
            skLineSegment(sketch, "E257.right", {"start": v(-308.64, -101.12) * mm, "end": v(-308.64, -106.12) * mm});
            skLineSegment(sketch, "E258.bottom", {"start": v(-297.75, -101.12) * mm, "end": v(-300.92, -101.12) * mm});
            skLineSegment(sketch, "E258.top", {"start": v(-297.75, -106.12) * mm, "end": v(-300.92, -106.12) * mm});
            skLineSegment(sketch, "E258.left", {"start": v(-297.75, -101.12) * mm, "end": v(-297.75, -106.12) * mm});
            skLineSegment(sketch, "E258.right", {"start": v(-300.92, -101.12) * mm, "end": v(-300.92, -106.12) * mm});
            skPoint(sketch, "E258.middle", {"position": v(-299.33, -103.62) * mm});
            skLineSegment(sketch, "E259.bottom", {"start": v(-290.03, -101.18) * mm, "end": v(-293.2, -101.18) * mm});
            skLineSegment(sketch, "E259.top", {"start": v(-290.03, -106.18) * mm, "end": v(-293.2, -106.18) * mm});
            skLineSegment(sketch, "E259.left", {"start": v(-290.03, -101.18) * mm, "end": v(-290.03, -106.18) * mm});
            skLineSegment(sketch, "E259.right", {"start": v(-293.2, -101.18) * mm, "end": v(-293.2, -106.18) * mm});
            skPoint(sketch, "E259.middle", {"position": v(-291.62, -103.68) * mm});
            skLineSegment(sketch, "E260.bottom", {"start": v(-282.31, -101.31) * mm, "end": v(-285.49, -101.31) * mm});
            skLineSegment(sketch, "E260.top", {"start": v(-282.31, -106.31) * mm, "end": v(-285.49, -106.31) * mm});
            skLineSegment(sketch, "E260.left", {"start": v(-282.31, -101.31) * mm, "end": v(-282.31, -106.31) * mm});
            skLineSegment(sketch, "E260.right", {"start": v(-285.49, -101.31) * mm, "end": v(-285.49, -106.31) * mm});
            skPoint(sketch, "E260.middle", {"position": v(-283.9, -103.81) * mm});
            skLineSegment(sketch, "E261.bottom", {"start": v(-307.28, -59.68) * mm, "end": v(-327.28, -59.68) * mm});
            skLineSegment(sketch, "E261.top", {"start": v(-307.28, -68.68) * mm, "end": v(-327.28, -68.68) * mm});
            skLineSegment(sketch, "E261.left", {"start": v(-307.28, -59.68) * mm, "end": v(-307.28, -68.68) * mm});
            skLineSegment(sketch, "E261.right", {"start": v(-327.28, -59.68) * mm, "end": v(-327.28, -68.68) * mm});
            skPoint(sketch, "E261.middle", {"position": v(-317.28, -64.18) * mm});
            skLineSegment(sketch, "E262", {"start": v(-307.28, -64.18) * mm, "end": v(-304.1, -64.18) * mm});
            skPoint(sketch, "E262.endSnap0", {"position": v(-307.28, -64.18) * mm});
            skLineSegment(sketch, "E263", {"start": v(-304.1, -64.18) * mm, "end": v(-304.1, -61.68) * mm});
            skLineSegment(sketch, "E264", {"start": v(-304.1, -61.68) * mm, "end": v(-307.28, -61.68) * mm});
            skLineSegment(sketch, "E265.MirrorCS", {"start": v(-304.1, -66.68) * mm, "end": v(-307.28, -66.68) * mm});
            skLineSegment(sketch, "E266.MirrorCS", {"start": v(-304.1, -64.18) * mm, "end": v(-304.1, -66.68) * mm});
            skLineSegment(sketch, "E267", {"start": v(-317.28, -68.68) * mm, "end": v(-317.28, -59.68) * mm});
            skLineSegment(sketch, "E268.MirrorCS", {"start": v(-330.46, -61.68) * mm, "end": v(-327.28, -61.68) * mm});
            skLineSegment(sketch, "E269.MirrorCS", {"start": v(-330.46, -64.18) * mm, "end": v(-330.46, -61.68) * mm});
            skLineSegment(sketch, "E270.MirrorCS", {"start": v(-330.46, -64.18) * mm, "end": v(-330.46, -66.68) * mm});
            skLineSegment(sketch, "E271.MirrorCS", {"start": v(-330.46, -66.68) * mm, "end": v(-327.28, -66.68) * mm});
            skLineSegment(sketch, "E272.MirrorCS", {"start": v(-327.28, -64.18) * mm, "end": v(-330.46, -64.18) * mm});
            skPoint(sketch, "E273", {"position": v(-223.3, -70.7) * mm});
            skPoint(sketch, "E274", {"position": v(-175.44, -183.52) * mm});
            skLineSegment(sketch, "E275", {"start": v(-184.83, -183.52) * mm, "end": v(-113.85, -218.14) * mm});
            skLineSegment(sketch, "E276", {"start": v(-175.77, -190.16) * mm, "end": v(-174.02, -186.57) * mm});
            skLineSegment(sketch, "E277", {"start": v(-174.02, -186.57) * mm, "end": v(-171.17, -187.96) * mm});
            skLineSegment(sketch, "E278", {"start": v(-171.17, -187.96) * mm, "end": v(-172.92, -191.55) * mm});
            skLineSegment(sketch, "E279", {"start": v(-172.92, -191.55) * mm, "end": v(-175.77, -190.16) * mm});
            skLineSegment(sketch, "E280", {"start": v(-168.5, -193.71) * mm, "end": v(-166.74, -190.12) * mm});
            skLineSegment(sketch, "E281", {"start": v(-166.74, -190.12) * mm, "end": v(-163.88, -191.5) * mm});
            skLineSegment(sketch, "E282", {"start": v(-163.88, -191.5) * mm, "end": v(-165.64, -195.1) * mm});
            skLineSegment(sketch, "E283", {"start": v(-165.64, -195.1) * mm, "end": v(-168.5, -193.71) * mm});
            skLineSegment(sketch, "E284", {"start": v(-159.46, -193.67) * mm, "end": v(-161.21, -197.26) * mm});
            skLineSegment(sketch, "E285", {"start": v(-161.21, -197.26) * mm, "end": v(-158.36, -198.65) * mm});
            skLineSegment(sketch, "E286", {"start": v(-158.36, -198.65) * mm, "end": v(-156.6, -195.06) * mm});
            skLineSegment(sketch, "E287", {"start": v(-156.6, -195.06) * mm, "end": v(-159.46, -193.67) * mm});
            skLineSegment(sketch, "E288", {"start": v(-152.09, -197.26) * mm, "end": v(-153.84, -200.86) * mm});
            skLineSegment(sketch, "E289", {"start": v(-153.84, -200.86) * mm, "end": v(-150.99, -202.25) * mm});
            skLineSegment(sketch, "E290", {"start": v(-150.99, -202.25) * mm, "end": v(-149.23, -198.65) * mm});
            skLineSegment(sketch, "E291", {"start": v(-149.23, -198.65) * mm, "end": v(-152.09, -197.26) * mm});
            skLineSegment(sketch, "E292", {"start": v(-143.64, -201.12) * mm, "end": v(-145.4, -204.71) * mm});
            skLineSegment(sketch, "E293", {"start": v(-145.4, -204.71) * mm, "end": v(-142.54, -206.1) * mm});
            skLineSegment(sketch, "E294", {"start": v(-142.54, -206.1) * mm, "end": v(-140.79, -202.5) * mm});
            skLineSegment(sketch, "E295", {"start": v(-140.79, -202.5) * mm, "end": v(-143.64, -201.12) * mm});
            skLineSegment(sketch, "E296", {"start": v(-138.25, -208.46) * mm, "end": v(-136.5, -204.86) * mm});
            skLineSegment(sketch, "E297", {"start": v(-136.5, -204.86) * mm, "end": v(-133.42, -206.36) * mm});
            skLineSegment(sketch, "E298", {"start": v(-133.42, -206.36) * mm, "end": v(-135.18, -209.96) * mm});
            skLineSegment(sketch, "E299", {"start": v(-135.18, -209.96) * mm, "end": v(-138.25, -208.46) * mm});
            skLineSegment(sketch, "E300", {"start": v(-130.18, -212.4) * mm, "end": v(-128.43, -208.8) * mm});
            skLineSegment(sketch, "E301", {"start": v(-128.43, -208.8) * mm, "end": v(-125.58, -210.2) * mm});
            skLineSegment(sketch, "E302", {"start": v(-125.58, -210.2) * mm, "end": v(-127.33, -213.79) * mm});
            skLineSegment(sketch, "E303", {"start": v(-127.33, -213.79) * mm, "end": v(-130.18, -212.4) * mm});
            skLineSegment(sketch, "E304.bottom", {"start": v(80.74, -8) * mm, "end": v(12.74, -8) * mm});
            skLineSegment(sketch, "E304.top", {"start": v(80.74, -30) * mm, "end": v(12.74, -30) * mm});
            skLineSegment(sketch, "E304.left", {"start": v(80.74, -8) * mm, "end": v(80.74, -30) * mm});
            skLineSegment(sketch, "E304.right", {"start": v(12.74, -8) * mm, "end": v(12.74, -30) * mm});
            skPoint(sketch, "E304.middle", {"position": v(46.74, -19) * mm});
            skPoint(sketch, "E304.middle.positionSnap0", {"position": v(46.74, -3) * mm});
            skPoint(sketch, "E304.middle.positionSnap1", {"position": v(7.74, -19) * mm});
            skPoint(sketch, "E304.centerSnap0", {"position": v(46.74, -3) * mm});
            skPoint(sketch, "E304.centerSnap1", {"position": v(7.74, -19) * mm});
            skLineSegment(sketch, "E305", {"start": v(12.74, -8) * mm, "end": v(80.74, -30) * mm, "construction": true});
            skLineSegment(sketch, "E306", {"start": v(80.74, -8) * mm, "end": v(12.74, -30) * mm, "construction": true});
            skLineSegment(sketch, "E307", {"start": v(12.74, -28.42) * mm, "end": v(75.87, -8) * mm});
            skLineSegment(sketch, "E308", {"start": v(17.61, -30) * mm, "end": v(80.74, -9.58) * mm});
            skLineSegment(sketch, "E309", {"start": v(12.74, -9.58) * mm, "end": v(75.87, -30) * mm});
            skLineSegment(sketch, "E310", {"start": v(17.61, -8) * mm, "end": v(80.74, -28.42) * mm});
            skLineSegment(sketch, "E311", {"start": v(15.42, -3) * mm, "end": v(22.27, 6.04) * mm});
            skLineSegment(sketch, "E312.MirrorCS", {"start": v(61.68, -3) * mm, "end": v(54.82, 6.04) * mm});
            skSolve(sketch);
        }
        {
            var Q0;
            {var subQ0=sQuery(id+"F0.wireOp",EDGE,"E229");var subQ3=sQuery(id+"F0.wireOp",EDGE,"E225");var subQ5=makeQuery(id+"F0.imprint","INTERSECT",VERTEX,{"derivedFrom":[subQ3,subQ0]});Q0=makeQuery(id+"F0.imprint","IMPRINT",FACE,{"disambiguationData":[TD([[makeQuery(id+"F0.imprint","IMPRINT",EDGE,{"disambiguationData":[TD([[subQ5,-1.0]])],"derivedFrom":subQ3}),1.0]])]});}
            var Q1;
            {var subQ0=sQuery(id+"F0.wireOp",EDGE,"E70");Q1=makeQuery(id+"F0.imprint","IMPRINT",FACE,{"disambiguationData":[TD([[makeQuery(id+"F0.imprint","IMPRINT",EDGE,{"derivedFrom":subQ0}),-1.0]])]});}
            var Q2;
            {var subQ16=sQuery(id+"F0.wireOp",EDGE,"E64.bottom");Q2=makeQuery(id+"F0.imprint","IMPRINT",FACE,{"disambiguationData":[TD([[makeQuery(id+"F0.imprint","IMPRINT",EDGE,{"derivedFrom":subQ16}),1.0]])]});}
            var Q3;
            {var subQ5=sQuery(id+"F0.wireOp",EDGE,"E94.left");var subQ6=sQuery(id+"F0.wireOp",EDGE,"E94.bottom");var subQ7=makeQuery(id+"F0.imprint","INTERSECT",VERTEX,{"derivedFrom":[subQ6,subQ5]});Q3=makeQuery(id+"F0.imprint","IMPRINT",FACE,{"disambiguationData":[TD([[makeQuery(id+"F0.imprint","IMPRINT",EDGE,{"disambiguationData":[TD([[subQ7,-1.0]])],"derivedFrom":subQ6}),1.0]])]});}
            var Q4;
            {var subQ1=sQuery(id+"F0.wireOp",EDGE,"E69");Q4=makeQuery(id+"F0.imprint","IMPRINT",FACE,{"disambiguationData":[TD([[makeQuery(id+"F0.imprint","IMPRINT",EDGE,{"derivedFrom":subQ1}),-1.0]])]});}
            var Q5;
            {var subQ0=sQuery(id+"F0.wireOp",EDGE,"E80.MirrorCS");Q5=makeQuery(id+"F0.imprint","IMPRINT",FACE,{"disambiguationData":[TD([[makeQuery(id+"F0.imprint","IMPRINT",EDGE,{"derivedFrom":subQ0}),1.0]])]});}
            var Q6;
            {var subQ1=sQuery(id+"F0.wireOp",EDGE,"E94.right");var subQ5=sQuery(id+"F0.wireOp",EDGE,"E94.bottom");var subQ6=makeQuery(id+"F0.imprint","INTERSECT",VERTEX,{"derivedFrom":[subQ5,subQ1]});Q6=makeQuery(id+"F0.imprint","IMPRINT",FACE,{"disambiguationData":[TD([[makeQuery(id+"F0.imprint","IMPRINT",EDGE,{"disambiguationData":[TD([[subQ6,1.0]])],"derivedFrom":subQ5}),1.0]])]});}
            var Q7;
            {var subQ0=sQuery(id+"F0.wireOp",EDGE,"E83.MirrorCS");Q7=makeQuery(id+"F0.imprint","IMPRINT",FACE,{"disambiguationData":[TD([[makeQuery(id+"F0.imprint","IMPRINT",EDGE,{"derivedFrom":subQ0}),1.0]])]});}
            var Q8;
            {var subQ2=sQuery(id+"F0.wireOp",EDGE,"E77.MirrorCS");Q8=makeQuery(id+"F0.imprint","IMPRINT",FACE,{"disambiguationData":[TD([[makeQuery(id+"F0.imprint","IMPRINT",EDGE,{"derivedFrom":subQ2}),1.0]])]});}
            var Q9;
            {var subQ1=sQuery(id+"F0.wireOp",EDGE,"E94.right");var subQ7=sQuery(id+"F0.wireOp",EDGE,"E94.top");var subQ8=makeQuery(id+"F0.imprint","INTERSECT",VERTEX,{"derivedFrom":[subQ7,subQ1]});Q9=makeQuery(id+"F0.imprint","IMPRINT",FACE,{"disambiguationData":[TD([[makeQuery(id+"F0.imprint","IMPRINT",EDGE,{"disambiguationData":[TD([[subQ8,1.0]])],"derivedFrom":subQ7}),-1.0]])]});}
            var Q10;
            {var subQ2=sQuery(id+"F0.wireOp",EDGE,"E86.MirrorCS");Q10=makeQuery(id+"F0.imprint","IMPRINT",FACE,{"disambiguationData":[TD([[makeQuery(id+"F0.imprint","IMPRINT",EDGE,{"derivedFrom":subQ2}),-1.0]])]});}
            var Q11;
            {var subQ0=sQuery(id+"F0.wireOp",EDGE,"E66");Q11=makeQuery(id+"F0.imprint","IMPRINT",FACE,{"disambiguationData":[TD([[makeQuery(id+"F0.imprint","IMPRINT",EDGE,{"derivedFrom":subQ0}),1.0]])]});}
            var Q12;
            {var subQ0=sQuery(id+"F0.wireOp",EDGE,"E73");Q12=makeQuery(id+"F0.imprint","IMPRINT",FACE,{"disambiguationData":[TD([[makeQuery(id+"F0.imprint","IMPRINT",EDGE,{"derivedFrom":subQ0}),-1.0]])]});}
            var Q13;
            {var subQ0=sQuery(id+"F0.wireOp",EDGE,"E99");var subQ1=sQuery(id+"F0.wireOp",EDGE,"E96");var subQ2=makeQuery(id+"F0.imprint","INTERSECT",VERTEX,{"derivedFrom":[subQ1,subQ0]});Q13=makeQuery(id+"F0.imprint","IMPRINT",FACE,{"disambiguationData":[TD([[makeQuery(id+"F0.imprint","IMPRINT",EDGE,{"disambiguationData":[TD([[subQ2,-1.0]])],"derivedFrom":subQ1}),-1.0]])]});}
            var Q14;
            {var subQ8=sQuery(id+"F0.wireOp",EDGE,"E16.left");Q14=makeQuery(id+"F0.imprint","IMPRINT",FACE,{"disambiguationData":[TD([[makeQuery(id+"F0.imprint","IMPRINT",EDGE,{"derivedFrom":subQ8}),-1.0]])]});}
            var Q15;
            {var subQ8=sQuery(id+"F0.wireOp",EDGE,"E16.left");Q15=makeQuery(id+"F0.imprint","IMPRINT",FACE,{"disambiguationData":[TD([[makeQuery(id+"F0.imprint","IMPRINT",EDGE,{"derivedFrom":subQ8}),-1.0]])]});}
            var Q16;
            {var subQ9=sQuery(id+"F0.wireOp",EDGE,"E135");Q16=makeQuery(id+"F0.imprint","IMPRINT",FACE,{"disambiguationData":[TD([[makeQuery(id+"F0.imprint","IMPRINT",EDGE,{"derivedFrom":subQ9}),-1.0]])]});}
            var Q17;
            {var subQ9=sQuery(id+"F0.wireOp",EDGE,"E135");Q17=makeQuery(id+"F0.imprint","IMPRINT",FACE,{"disambiguationData":[TD([[makeQuery(id+"F0.imprint","IMPRINT",EDGE,{"derivedFrom":subQ9}),-1.0]])]});}
            var Q18;
            {var subQ2=sQuery(id+"F0.wireOp",EDGE,"E44");Q18=makeQuery(id+"F0.imprint","IMPRINT",FACE,{"disambiguationData":[TD([[makeQuery(id+"F0.imprint","IMPRINT",EDGE,{"derivedFrom":subQ2}),1.0]])]});}
            var Q19;
            {var subQ0=sQuery(id+"F0.wireOp",EDGE,"E41");Q19=makeQuery(id+"F0.imprint","IMPRINT",FACE,{"disambiguationData":[TD([[makeQuery(id+"F0.imprint","IMPRINT",EDGE,{"derivedFrom":subQ0}),1.0]])]});}
            var Q20;
            {var subQ0=sQuery(id+"F0.wireOp",EDGE,"E35");Q20=makeQuery(id+"F0.imprint","IMPRINT",FACE,{"disambiguationData":[TD([[makeQuery(id+"F0.imprint","IMPRINT",EDGE,{"derivedFrom":subQ0}),1.0]])]});}
            var Q21;
            {var subQ0=sQuery(id+"F0.wireOp",EDGE,"E32");Q21=makeQuery(id+"F0.imprint","IMPRINT",FACE,{"disambiguationData":[TD([[makeQuery(id+"F0.imprint","IMPRINT",EDGE,{"derivedFrom":subQ0}),1.0]])]});}
            var Q22;
            {var subQ0=sQuery(id+"F0.wireOp",EDGE,"E38");Q22=makeQuery(id+"F0.imprint","IMPRINT",FACE,{"disambiguationData":[TD([[makeQuery(id+"F0.imprint","IMPRINT",EDGE,{"derivedFrom":subQ0}),1.0]])]});}
            var Q23;
            Q23=makeQuery(id+"F0.imprint","IMPRINT",FACE,{"disambiguationData":[TD([[makeQuery(id+"F0.imprint","IMPRINT",EDGE,{"derivedFrom":sQuery(id+"F0.wireOp",EDGE,"E16.bottom")}),-1.0]])]});
            var Q24;
            {var subQ1=sQuery(id+"F0.wireOp",EDGE,"E4");Q24=makeQuery(id+"F0.imprint","IMPRINT",FACE,{"disambiguationData":[TD([[makeQuery(id+"F0.imprint","IMPRINT",EDGE,{"derivedFrom":subQ1}),-1.0]])]});}
            var Q25;
            {var subQ0=sQuery(id+"F0.wireOp",EDGE,"E12.MirrorCS");Q25=makeQuery(id+"F0.imprint","IMPRINT",FACE,{"disambiguationData":[TD([[makeQuery(id+"F0.imprint","IMPRINT",EDGE,{"derivedFrom":subQ0}),1.0]])]});}
            var Q26;
            {var subQ0=sQuery(id+"F0.wireOp",EDGE,"E9.MirrorCS");Q26=makeQuery(id+"F0.imprint","IMPRINT",FACE,{"disambiguationData":[TD([[makeQuery(id+"F0.imprint","IMPRINT",EDGE,{"derivedFrom":subQ0}),-1.0]])]});}
            var Q27;
            {var subQ0=sQuery(id+"F0.wireOp",EDGE,"E29");Q27=makeQuery(id+"F0.imprint","IMPRINT",FACE,{"disambiguationData":[TD([[makeQuery(id+"F0.imprint","IMPRINT",EDGE,{"derivedFrom":subQ0}),1.0]])]});}
            var Q28;
            {var subQ0=sQuery(id+"F0.wireOp",EDGE,"E26");Q28=makeQuery(id+"F0.imprint","IMPRINT",FACE,{"disambiguationData":[TD([[makeQuery(id+"F0.imprint","IMPRINT",EDGE,{"derivedFrom":subQ0}),1.0]])]});}
            var Q29;
            {var subQ0=sQuery(id+"F0.wireOp",EDGE,"E20");Q29=makeQuery(id+"F0.imprint","IMPRINT",FACE,{"disambiguationData":[TD([[makeQuery(id+"F0.imprint","IMPRINT",EDGE,{"derivedFrom":subQ0}),1.0]])]});}
            var Q30;
            {var subQ1=sQuery(id+"F0.wireOp",EDGE,"E5");Q30=makeQuery(id+"F0.imprint","IMPRINT",FACE,{"disambiguationData":[TD([[makeQuery(id+"F0.imprint","IMPRINT",EDGE,{"derivedFrom":subQ1}),-1.0]])]});}
            var Q31;
            Q31=makeQuery(id+"F0.imprint","IMPRINT",FACE,{"disambiguationData":[TD([[makeQuery(id+"F0.imprint","IMPRINT",EDGE,{"derivedFrom":sQuery(id+"F0.wireOp",EDGE,"E0.right")}),-1.0]])]});
            var Q32;
            {var subQ1=sQuery(id+"F0.wireOp",EDGE,"E0.left");Q32=makeQuery(id+"F0.imprint","IMPRINT",FACE,{"disambiguationData":[TD([[makeQuery(id+"F0.imprint","IMPRINT",EDGE,{"derivedFrom":subQ1}),-1.0]])]});}
            var Q33;
            {var subQ3=sQuery(id+"F0.wireOp",EDGE,"E51");Q33=makeQuery(id+"F0.imprint","IMPRINT",FACE,{"disambiguationData":[TD([[makeQuery(id+"F0.imprint","IMPRINT",EDGE,{"derivedFrom":subQ3}),1.0]])]});}
            var Q34;
            {var subQ0=sQuery(id+"F0.wireOp",EDGE,"E52");Q34=makeQuery(id+"F0.imprint","IMPRINT",FACE,{"disambiguationData":[TD([[makeQuery(id+"F0.imprint","IMPRINT",EDGE,{"derivedFrom":subQ0}),1.0]])]});}
            var Q35;
            {var subQ0=sQuery(id+"F0.wireOp",EDGE,"E58");Q35=makeQuery(id+"F0.imprint","IMPRINT",FACE,{"disambiguationData":[TD([[makeQuery(id+"F0.imprint","IMPRINT",EDGE,{"derivedFrom":subQ0}),1.0]])]});}
            var Q36;
            {var subQ0=sQuery(id+"F0.wireOp",EDGE,"E61");Q36=makeQuery(id+"F0.imprint","IMPRINT",FACE,{"disambiguationData":[TD([[makeQuery(id+"F0.imprint","IMPRINT",EDGE,{"derivedFrom":subQ0}),1.0]])]});}
            var Q37;
            Q37=makeQuery(id+"F0.imprint","IMPRINT",FACE,{"disambiguationData":[TD([[makeQuery(id+"F0.imprint","IMPRINT",EDGE,{"derivedFrom":sQuery(id+"F0.wireOp",EDGE,"E49.MirrorCS")}),-1.0]])]});
            var Q38;
            {var subQ1=sQuery(id+"F0.wireOp",EDGE,"E102.left");var subQ6=sQuery(id+"F0.wireOp",EDGE,"E102.top");var subQ9=makeQuery(id+"F0.imprint","INTERSECT",VERTEX,{"derivedFrom":[subQ6,subQ1]});Q38=makeQuery(id+"F0.imprint","IMPRINT",FACE,{"disambiguationData":[TD([[makeQuery(id+"F0.imprint","IMPRINT",EDGE,{"disambiguationData":[TD([[subQ9,-1.0]])],"derivedFrom":subQ6}),-1.0]])]});}
            var Q39;
            {var subQ1=sQuery(id+"F0.wireOp",EDGE,"E102.right");var subQ5=sQuery(id+"F0.wireOp",EDGE,"E102.top");var subQ6=makeQuery(id+"F0.imprint","INTERSECT",VERTEX,{"derivedFrom":[subQ5,subQ1]});Q39=makeQuery(id+"F0.imprint","IMPRINT",FACE,{"disambiguationData":[TD([[makeQuery(id+"F0.imprint","IMPRINT",EDGE,{"disambiguationData":[TD([[subQ6,1.0]])],"derivedFrom":subQ5}),-1.0]])]});}
            var Q40;
            {var subQ0=sQuery(id+"F0.wireOp",EDGE,"E55");Q40=makeQuery(id+"F0.imprint","IMPRINT",FACE,{"disambiguationData":[TD([[makeQuery(id+"F0.imprint","IMPRINT",EDGE,{"derivedFrom":subQ0}),1.0]])]});}
            var Q41;
            {var subQ5=sQuery(id+"F0.wireOp",EDGE,"E102.left");var subQ6=sQuery(id+"F0.wireOp",EDGE,"E102.bottom");var subQ7=makeQuery(id+"F0.imprint","INTERSECT",VERTEX,{"derivedFrom":[subQ6,subQ5]});Q41=makeQuery(id+"F0.imprint","IMPRINT",FACE,{"disambiguationData":[TD([[makeQuery(id+"F0.imprint","IMPRINT",EDGE,{"disambiguationData":[TD([[subQ7,-1.0]])],"derivedFrom":subQ6}),1.0]])]});}
            var Q42;
            {var subQ1=sQuery(id+"F0.wireOp",EDGE,"E102.bottom");var subQ5=sQuery(id+"F0.wireOp",EDGE,"E102.right");var subQ6=makeQuery(id+"F0.imprint","INTERSECT",VERTEX,{"derivedFrom":[subQ1,subQ5]});Q42=makeQuery(id+"F0.imprint","IMPRINT",FACE,{"disambiguationData":[TD([[makeQuery(id+"F0.imprint","IMPRINT",EDGE,{"disambiguationData":[TD([[subQ6,1.0]])],"derivedFrom":subQ1}),1.0]])]});}
            var Q43;
            Q43=makeQuery(id+"F0.imprint","IMPRINT",FACE,{"disambiguationData":[TD([[makeQuery(id+"F0.imprint","IMPRINT",EDGE,{"derivedFrom":sQuery(id+"F0.wireOp",EDGE,"E50.MirrorCS")}),1.0]])]});
            var Q44;
            {var subQ0=sQuery(id+"F0.wireOp",EDGE,"E113");var subQ1=sQuery(id+"F0.wireOp",EDGE,"E111");var subQ2=makeQuery(id+"F0.imprint","INTERSECT",VERTEX,{"derivedFrom":[subQ1,subQ0]});Q44=makeQuery(id+"F0.imprint","IMPRINT",FACE,{"disambiguationData":[TD([[makeQuery(id+"F0.imprint","IMPRINT",EDGE,{"disambiguationData":[TD([[subQ2,-1.0]])],"derivedFrom":subQ1}),1.0]])]});}
            var Q45;
            Q45=makeQuery(id+"F0.imprint","IMPRINT",FACE,{"disambiguationData":[TD([[makeQuery(id+"F0.imprint","IMPRINT",EDGE,{"derivedFrom":sQuery(id+"F0.wireOp",EDGE,"E0.left")}),1.0]])]});
            var Q46;
            {var subQ4=sQuery(id+"F0.wireOp",EDGE,"E157");var subQ7=makeQuery(id+"F0.imprint","IMPRINT",VERTEX,{"derivedFrom":subQ4});Q46=makeQuery(id+"F0.imprint","IMPRINT",FACE,{"disambiguationData":[TD([[makeQuery(id+"F0.imprint","IMPRINT",EDGE,{"disambiguationData":[TD([[subQ7,-1.0]])],"derivedFrom":subQ4}),-1.0]])]});}
            var Q47;
            {var subQ0=sQuery(id+"F0.wireOp",EDGE,"E144");Q47=makeQuery(id+"F0.imprint","IMPRINT",FACE,{"disambiguationData":[TD([[makeQuery(id+"F0.imprint","IMPRINT",EDGE,{"derivedFrom":subQ0}),1.0]])]});}
            var Q48;
            {var subQ0=sQuery(id+"F0.wireOp",EDGE,"E147");Q48=makeQuery(id+"F0.imprint","IMPRINT",FACE,{"disambiguationData":[TD([[makeQuery(id+"F0.imprint","IMPRINT",EDGE,{"derivedFrom":subQ0}),1.0]])]});}
            var Q49;
            {var subQ0=sQuery(id+"F0.wireOp",EDGE,"E150");Q49=makeQuery(id+"F0.imprint","IMPRINT",FACE,{"disambiguationData":[TD([[makeQuery(id+"F0.imprint","IMPRINT",EDGE,{"derivedFrom":subQ0}),1.0]])]});}
            var Q50;
            {var subQ0=sQuery(id+"F0.wireOp",EDGE,"E153");Q50=makeQuery(id+"F0.imprint","IMPRINT",FACE,{"disambiguationData":[TD([[makeQuery(id+"F0.imprint","IMPRINT",EDGE,{"derivedFrom":subQ0}),1.0]])]});}
            var Q51;
            Q51=makeQuery(id+"F0.imprint","IMPRINT",FACE,{"disambiguationData":[TD([[makeQuery(id+"F0.imprint","IMPRINT",EDGE,{"derivedFrom":sQuery(id+"F0.wireOp",EDGE,"E142.MirrorCS")}),1.0]])]});
            var Q52;
            Q52=makeQuery(id+"F0.imprint","IMPRINT",FACE,{"disambiguationData":[TD([[makeQuery(id+"F0.imprint","IMPRINT",EDGE,{"derivedFrom":sQuery(id+"F0.wireOp",EDGE,"E141.MirrorCS")}),-1.0]])]});
            var Q53;
            Q53=makeQuery(id+"F0.imprint","IMPRINT",FACE,{"disambiguationData":[TD([[makeQuery(id+"F0.imprint","IMPRINT",EDGE,{"derivedFrom":sQuery(id+"F0.wireOp",EDGE,"E174.bottom")}),-1.0]])]});
            var Q54;
            {var subQ0=sQuery(id+"F0.wireOp",EDGE,"E174.left");Q54=makeQuery(id+"F0.imprint","IMPRINT",FACE,{"disambiguationData":[TD([[makeQuery(id+"F0.imprint","IMPRINT",EDGE,{"derivedFrom":subQ0}),-1.0]])]});}
            var Q55;
            {var subQ5=sQuery(id+"F0.wireOp",EDGE,"E178.top");Q55=makeQuery(id+"F0.imprint","IMPRINT",FACE,{"disambiguationData":[TD([[makeQuery(id+"F0.imprint","IMPRINT",EDGE,{"derivedFrom":subQ5}),-1.0]])]});}
            var Q56;
            {var subQ5=sQuery(id+"F0.wireOp",EDGE,"E178.bottom");Q56=makeQuery(id+"F0.imprint","IMPRINT",FACE,{"disambiguationData":[TD([[makeQuery(id+"F0.imprint","IMPRINT",EDGE,{"derivedFrom":subQ5}),1.0]])]});}
            var Q57;
            {var subQ15=sQuery(id+"F0.wireOp",EDGE,"E2.top");var subQ20=makeQuery(id+"F0.imprint","INTERSECT",VERTEX,{"derivedFrom":[subQ15,sQuery(id+"F0.wireOp",EDGE,"E38")]});Q57=makeQuery(id+"F0.imprint","IMPRINT",FACE,{"disambiguationData":[TD([[makeQuery(id+"F0.imprint","IMPRINT",EDGE,{"disambiguationData":[TD([[subQ20,1.0]])],"derivedFrom":subQ15}),-1.0]])]});}
            var Q58;
            {var subQ11=sQuery(id+"F0.wireOp",EDGE,"E2.bottom");var subQ18=makeQuery(id+"F0.imprint","INTERSECT",VERTEX,{"derivedFrom":[subQ11,sQuery(id+"F0.wireOp",EDGE,"E192.MirrorCS")]});Q58=makeQuery(id+"F0.imprint","IMPRINT",FACE,{"disambiguationData":[TD([[makeQuery(id+"F0.imprint","IMPRINT",EDGE,{"disambiguationData":[TD([[subQ18,1.0]])],"derivedFrom":subQ11}),1.0]])]});}
            var Q59;
            Q59=makeQuery(id+"F0.imprint","IMPRINT",FACE,{"disambiguationData":[TD([[makeQuery(id+"F0.imprint","IMPRINT",EDGE,{"derivedFrom":sQuery(id+"F0.wireOp",EDGE,"E188.MirrorCS")}),-1.0]])]});
            var Q60;
            Q60=makeQuery(id+"F0.imprint","IMPRINT",FACE,{"disambiguationData":[TD([[makeQuery(id+"F0.imprint","IMPRINT",EDGE,{"derivedFrom":sQuery(id+"F0.wireOp",EDGE,"E185.MirrorCS")}),-1.0]])]});
            var Q61;
            {var subQ0=sQuery(id+"F0.wireOp",EDGE,"E192.MirrorCS");Q61=makeQuery(id+"F0.imprint","IMPRINT",FACE,{"disambiguationData":[TD([[makeQuery(id+"F0.imprint","IMPRINT",EDGE,{"derivedFrom":subQ0}),-1.0]])]});}
            var Q62;
            {var subQ0=sQuery(id+"F0.wireOp",EDGE,"E193.MirrorCS");Q62=makeQuery(id+"F0.imprint","IMPRINT",FACE,{"disambiguationData":[TD([[makeQuery(id+"F0.imprint","IMPRINT",EDGE,{"derivedFrom":subQ0}),-1.0]])]});}
            var Q63;
            Q63=makeQuery(id+"F0.imprint","IMPRINT",FACE,{"disambiguationData":[TD([[makeQuery(id+"F0.imprint","IMPRINT",EDGE,{"derivedFrom":sQuery(id+"F0.wireOp",EDGE,"E194.MirrorCS")}),-1.0]])]});
            var Q64;
            {var subQ2=sQuery(id+"F0.wireOp",EDGE,"E197.MirrorCS");Q64=makeQuery(id+"F0.imprint","IMPRINT",FACE,{"disambiguationData":[TD([[makeQuery(id+"F0.imprint","IMPRINT",EDGE,{"derivedFrom":subQ2}),-1.0]])]});}
            var Q65;
            {var subQ0=sQuery(id+"F0.wireOp",EDGE,"E200.MirrorCS");Q65=makeQuery(id+"F0.imprint","IMPRINT",FACE,{"disambiguationData":[TD([[makeQuery(id+"F0.imprint","IMPRINT",EDGE,{"derivedFrom":subQ0}),-1.0]])]});}
            var Q66;
            {var subQ0=sQuery(id+"F0.wireOp",EDGE,"E40");Q66=makeQuery(id+"F0.imprint","IMPRINT",FACE,{"disambiguationData":[TD([[makeQuery(id+"F0.imprint","IMPRINT",EDGE,{"derivedFrom":subQ0}),1.0]])]});}
            var Q67;
            {var subQ0=sQuery(id+"F0.wireOp",EDGE,"nwX5COAi-Dhrm-Zb6F-e9EF-I4LykCu5jgMt.left");Q67=makeQuery(id+"F0.imprint","IMPRINT",FACE,{"disambiguationData":[TD([[makeQuery(id+"F0.imprint","IMPRINT",EDGE,{"derivedFrom":subQ0}),-1.0]])]});}
            var Q68;
            {var subQ4=sQuery(id+"F0.wireOp",EDGE,"nwX5COAi-Dhrm-Zb6F-e9EF-I4LykCu5jgMt.left");Q68=makeQuery(id+"F0.imprint","IMPRINT",FACE,{"disambiguationData":[TD([[makeQuery(id+"F0.imprint","IMPRINT",EDGE,{"derivedFrom":subQ4}),1.0]])]});}
            var Q69;
            {var subQ6=sQuery(id+"F0.wireOp",EDGE,"jegdBQM5-Uewl-We8a-Z8K1-QPvYAGG4aklX");Q69=makeQuery(id+"F0.imprint","IMPRINT",FACE,{"disambiguationData":[TD([[makeQuery(id+"F0.imprint","IMPRINT",EDGE,{"derivedFrom":subQ6}),-1.0]])]});}
            var Q70;
            {var subQ0=sQuery(id+"F0.wireOp",EDGE,"Y8Zzet1n-i3AM-vDlW-kn0r-yr2E13k5ydEb");Q70=makeQuery(id+"F0.imprint","IMPRINT",FACE,{"disambiguationData":[TD([[makeQuery(id+"F0.imprint","IMPRINT",EDGE,{"derivedFrom":subQ0}),-1.0]])]});}
            var Q71;
            {var subQ5=sQuery(id+"F0.wireOp",EDGE,"E217.bottom");Q71=makeQuery(id+"F0.imprint","IMPRINT",FACE,{"disambiguationData":[TD([[makeQuery(id+"F0.imprint","IMPRINT",EDGE,{"derivedFrom":subQ5}),1.0]])]});}
            var Q72;
            {var subQ5=sQuery(id+"F0.wireOp",EDGE,"E217.top");Q72=makeQuery(id+"F0.imprint","IMPRINT",FACE,{"disambiguationData":[TD([[makeQuery(id+"F0.imprint","IMPRINT",EDGE,{"derivedFrom":subQ5}),-1.0]])]});}
            var Q73;
            {var subQ12=sQuery(id+"F0.wireOp",EDGE,"E213.left");Q73=makeQuery(id+"F0.imprint","IMPRINT",FACE,{"disambiguationData":[TD([[makeQuery(id+"F0.imprint","IMPRINT",EDGE,{"derivedFrom":subQ12}),-1.0]])]});}
            var Q74;
            {var subQ0=sQuery(id+"F0.wireOp",EDGE,"OAm9FsYN-pAe9-ynBv-Xqhv-jLcd5oZKLZ71");Q74=makeQuery(id+"F0.imprint","IMPRINT",FACE,{"disambiguationData":[TD([[makeQuery(id+"F0.imprint","IMPRINT",EDGE,{"derivedFrom":subQ0}),1.0]])]});}
            var Q75;
            Q75=makeQuery(id+"F0.imprint","IMPRINT",FACE,{"disambiguationData":[TD([[makeQuery(id+"F0.imprint","IMPRINT",EDGE,{"derivedFrom":sQuery(id+"F0.wireOp",EDGE,"E213.bottom")}),-1.0]])]});
            var Q76;
            {var subQ0=sQuery(id+"F0.wireOp",EDGE,"E221.MirrorCS");Q76=makeQuery(id+"F0.imprint","IMPRINT",FACE,{"disambiguationData":[TD([[makeQuery(id+"F0.imprint","IMPRINT",EDGE,{"derivedFrom":subQ0}),1.0]])]});}
            var Q77;
            {var subQ14=sQuery(id+"F0.wireOp",EDGE,"E219.left");Q77=makeQuery(id+"F0.imprint","IMPRINT",FACE,{"disambiguationData":[TD([[makeQuery(id+"F0.imprint","IMPRINT",EDGE,{"derivedFrom":subQ14}),-1.0]])]});}
            var Q78;
            Q78=makeQuery(id+"F0.imprint","IMPRINT",FACE,{"disambiguationData":[TD([[makeQuery(id+"F0.imprint","IMPRINT",EDGE,{"derivedFrom":sQuery(id+"F0.wireOp",EDGE,"E219.bottom")}),-1.0]])]});
            var Q79;
            {var subQ4=sQuery(id+"F0.wireOp",EDGE,"E218.right");var subQ5=sQuery(id+"F0.wireOp",EDGE,"E218.bottom");var subQ6=makeQuery(id+"F0.imprint","INTERSECT",VERTEX,{"derivedFrom":[subQ5,subQ4]});Q79=makeQuery(id+"F0.imprint","IMPRINT",FACE,{"disambiguationData":[TD([[makeQuery(id+"F0.imprint","IMPRINT",EDGE,{"disambiguationData":[TD([[subQ6,1.0]])],"derivedFrom":subQ5}),1.0]])]});}
            var Q80;
            {var subQ1=sQuery(id+"F0.wireOp",EDGE,"E224.right");var subQ3=sQuery(id+"F0.wireOp",EDGE,"E227");var subQ4=makeQuery(id+"F0.imprint","INTERSECT",VERTEX,{"derivedFrom":[subQ1,subQ3]});Q80=makeQuery(id+"F0.imprint","IMPRINT",FACE,{"disambiguationData":[TD([[makeQuery(id+"F0.imprint","IMPRINT",EDGE,{"disambiguationData":[TD([[subQ4,-1.0]])],"derivedFrom":subQ3}),1.0]])]});}
            var Q81;
            {var subQ1=sQuery(id+"F0.wireOp",EDGE,"E224.bottom");var subQ3=sQuery(id+"F0.wireOp",EDGE,"E228");var subQ4=makeQuery(id+"F0.imprint","INTERSECT",VERTEX,{"derivedFrom":[subQ1,subQ3]});Q81=makeQuery(id+"F0.imprint","IMPRINT",FACE,{"disambiguationData":[TD([[makeQuery(id+"F0.imprint","IMPRINT",EDGE,{"disambiguationData":[TD([[subQ4,-1.0]])],"derivedFrom":subQ1}),1.0]])]});}
            var Q82;
            {var subQ3=sQuery(id+"F0.wireOp",EDGE,"E226");var subQ5=sQuery(id+"F0.wireOp",EDGE,"E227");var subQ6=makeQuery(id+"F0.imprint","INTERSECT",VERTEX,{"derivedFrom":[subQ3,subQ5]});Q82=makeQuery(id+"F0.imprint","IMPRINT",FACE,{"disambiguationData":[TD([[makeQuery(id+"F0.imprint","IMPRINT",EDGE,{"disambiguationData":[TD([[subQ6,1.0]])],"derivedFrom":subQ5}),1.0]])]});}
            var Q83;
            {var subQ1=sQuery(id+"F0.wireOp",EDGE,"E224.top");var subQ3=sQuery(id+"F0.wireOp",EDGE,"E227");var subQ4=makeQuery(id+"F0.imprint","INTERSECT",VERTEX,{"derivedFrom":[subQ1,subQ3]});Q83=makeQuery(id+"F0.imprint","IMPRINT",FACE,{"disambiguationData":[TD([[makeQuery(id+"F0.imprint","IMPRINT",EDGE,{"disambiguationData":[TD([[subQ4,1.0]])],"derivedFrom":subQ1}),-1.0]])]});}
            var Q84;
            {var subQ1=sQuery(id+"F0.wireOp",EDGE,"E224.left");var subQ3=sQuery(id+"F0.wireOp",EDGE,"E228");var subQ4=makeQuery(id+"F0.imprint","INTERSECT",VERTEX,{"derivedFrom":[subQ1,subQ3]});Q84=makeQuery(id+"F0.imprint","IMPRINT",FACE,{"disambiguationData":[TD([[makeQuery(id+"F0.imprint","IMPRINT",EDGE,{"disambiguationData":[TD([[subQ4,1.0]])],"derivedFrom":subQ3}),-1.0]])]});}
            var Q85;
            {var subQ1=sQuery(id+"F0.wireOp",EDGE,"E224.bottom");var subQ3=sQuery(id+"F0.wireOp",EDGE,"E229");var subQ4=makeQuery(id+"F0.imprint","INTERSECT",VERTEX,{"derivedFrom":[subQ1,subQ3]});Q85=makeQuery(id+"F0.imprint","IMPRINT",FACE,{"disambiguationData":[TD([[makeQuery(id+"F0.imprint","IMPRINT",EDGE,{"disambiguationData":[TD([[subQ4,1.0]])],"derivedFrom":subQ1}),1.0]])]});}
            var Q86;
            {var subQ0=sQuery(id+"F0.wireOp",EDGE,"E226");var subQ5=sQuery(id+"F0.wireOp",EDGE,"E228");var subQ6=makeQuery(id+"F0.imprint","INTERSECT",VERTEX,{"derivedFrom":[subQ0,subQ5]});Q86=makeQuery(id+"F0.imprint","IMPRINT",FACE,{"disambiguationData":[TD([[makeQuery(id+"F0.imprint","IMPRINT",EDGE,{"disambiguationData":[TD([[subQ6,-1.0]])],"derivedFrom":subQ5}),1.0]])]});}
            var Q87;
            {var subQ0=sQuery(id+"F0.wireOp",EDGE,"E228");var subQ3=sQuery(id+"F0.wireOp",EDGE,"E226");var subQ5=makeQuery(id+"F0.imprint","INTERSECT",VERTEX,{"derivedFrom":[subQ3,subQ0]});Q87=makeQuery(id+"F0.imprint","IMPRINT",FACE,{"disambiguationData":[TD([[makeQuery(id+"F0.imprint","IMPRINT",EDGE,{"disambiguationData":[TD([[subQ5,-1.0]])],"derivedFrom":subQ3}),-1.0]])]});}
            var Q88;
            {var subQ3=sQuery(id+"F0.wireOp",EDGE,"E226");var subQ5=sQuery(id+"F0.wireOp",EDGE,"E228");var subQ6=makeQuery(id+"F0.imprint","INTERSECT",VERTEX,{"derivedFrom":[subQ3,subQ5]});Q88=makeQuery(id+"F0.imprint","IMPRINT",FACE,{"disambiguationData":[TD([[makeQuery(id+"F0.imprint","IMPRINT",EDGE,{"disambiguationData":[TD([[subQ6,-1.0]])],"derivedFrom":subQ5}),-1.0]])]});}
            var Q89;
            {var subQ0=sQuery(id+"F0.wireOp",EDGE,"E227");var subQ3=sQuery(id+"F0.wireOp",EDGE,"E226");var subQ5=makeQuery(id+"F0.imprint","INTERSECT",VERTEX,{"derivedFrom":[subQ3,subQ0]});Q89=makeQuery(id+"F0.imprint","IMPRINT",FACE,{"disambiguationData":[TD([[makeQuery(id+"F0.imprint","IMPRINT",EDGE,{"disambiguationData":[TD([[subQ5,1.0]])],"derivedFrom":subQ3}),1.0]])]});}
            var Q90;
            {var subQ0=sQuery(id+"F0.wireOp",EDGE,"xSubQ0ot-JDVd-ggLh-KBvV-1MOrFfWz392f");var subQ3=sQuery(id+"F0.wireOp",EDGE,"E225");var subQ5=makeQuery(id+"F0.imprint","INTERSECT",VERTEX,{"derivedFrom":[subQ3,subQ0]});Q90=makeQuery(id+"F0.imprint","IMPRINT",FACE,{"disambiguationData":[TD([[makeQuery(id+"F0.imprint","IMPRINT",EDGE,{"disambiguationData":[TD([[subQ5,1.0]])],"derivedFrom":subQ3}),-1.0]])]});}
            var Q91;
            {var subQ0=sQuery(id+"F0.wireOp",EDGE,"E226");var subQ5=sQuery(id+"F0.wireOp",EDGE,"E227");var subQ6=makeQuery(id+"F0.imprint","INTERSECT",VERTEX,{"derivedFrom":[subQ0,subQ5]});Q91=makeQuery(id+"F0.imprint","IMPRINT",FACE,{"disambiguationData":[TD([[makeQuery(id+"F0.imprint","IMPRINT",EDGE,{"disambiguationData":[TD([[subQ6,1.0]])],"derivedFrom":subQ5}),-1.0]])]});}
            var Q92;
            {var subQ1=sQuery(id+"F0.wireOp",EDGE,"E224.top");var subQ3=sQuery(id+"F0.wireOp",EDGE,"E230");var subQ4=makeQuery(id+"F0.imprint","INTERSECT",VERTEX,{"derivedFrom":[subQ1,subQ3]});Q92=makeQuery(id+"F0.imprint","IMPRINT",FACE,{"disambiguationData":[TD([[makeQuery(id+"F0.imprint","IMPRINT",EDGE,{"disambiguationData":[TD([[subQ4,-1.0]])],"derivedFrom":subQ1}),-1.0]])]});}
            var Q93;
            {var subQ0=sQuery(id+"F0.wireOp",EDGE,"E224.bottom");var subQ3=sQuery(id+"F0.wireOp",EDGE,"E228");var subQ5=makeQuery(id+"F0.imprint","INTERSECT",VERTEX,{"derivedFrom":[subQ0,subQ3]});Q93=makeQuery(id+"F0.imprint","IMPRINT",FACE,{"disambiguationData":[TD([[makeQuery(id+"F0.imprint","IMPRINT",EDGE,{"disambiguationData":[TD([[subQ5,1.0]])],"derivedFrom":subQ0}),1.0]])]});}
            var Q94;
            {var subQ0=sQuery(id+"F0.wireOp",EDGE,"E227");var subQ1=sQuery(id+"F0.wireOp",EDGE,"E224.right");var subQ2=makeQuery(id+"F0.imprint","INTERSECT",VERTEX,{"derivedFrom":[subQ1,subQ0]});Q94=makeQuery(id+"F0.imprint","IMPRINT",FACE,{"disambiguationData":[TD([[makeQuery(id+"F0.imprint","IMPRINT",EDGE,{"disambiguationData":[TD([[subQ2,-1.0]])],"derivedFrom":subQ1}),1.0]])]});}
            var Q95;
            {var subQ0=sQuery(id+"F0.wireOp",EDGE,"E224.bottom");var subQ3=sQuery(id+"F0.wireOp",EDGE,"E229");var subQ5=makeQuery(id+"F0.imprint","INTERSECT",VERTEX,{"derivedFrom":[subQ0,subQ3]});Q95=makeQuery(id+"F0.imprint","IMPRINT",FACE,{"disambiguationData":[TD([[makeQuery(id+"F0.imprint","IMPRINT",EDGE,{"disambiguationData":[TD([[subQ5,-1.0]])],"derivedFrom":subQ0}),1.0]])]});}
            var Q96;
            {var subQ0=sQuery(id+"F0.wireOp",EDGE,"E228");var subQ1=sQuery(id+"F0.wireOp",EDGE,"E224.left");var subQ2=makeQuery(id+"F0.imprint","INTERSECT",VERTEX,{"derivedFrom":[subQ1,subQ0]});Q96=makeQuery(id+"F0.imprint","IMPRINT",FACE,{"disambiguationData":[TD([[makeQuery(id+"F0.imprint","IMPRINT",EDGE,{"disambiguationData":[TD([[subQ2,1.0]])],"derivedFrom":subQ1}),-1.0]])]});}
            var Q97;
            {var subQ0=sQuery(id+"F0.wireOp",EDGE,"E224.top");var subQ3=sQuery(id+"F0.wireOp",EDGE,"E227");var subQ5=makeQuery(id+"F0.imprint","INTERSECT",VERTEX,{"derivedFrom":[subQ0,subQ3]});Q97=makeQuery(id+"F0.imprint","IMPRINT",FACE,{"disambiguationData":[TD([[makeQuery(id+"F0.imprint","IMPRINT",EDGE,{"disambiguationData":[TD([[subQ5,-1.0]])],"derivedFrom":subQ0}),-1.0]])]});}
            var Q98;
            {var subQ0=sQuery(id+"F0.wireOp",EDGE,"E224.top");var subQ3=sQuery(id+"F0.wireOp",EDGE,"E230");var subQ5=makeQuery(id+"F0.imprint","INTERSECT",VERTEX,{"derivedFrom":[subQ0,subQ3]});Q98=makeQuery(id+"F0.imprint","IMPRINT",FACE,{"disambiguationData":[TD([[makeQuery(id+"F0.imprint","IMPRINT",EDGE,{"disambiguationData":[TD([[subQ5,1.0]])],"derivedFrom":subQ0}),-1.0]])]});}
            var Q99;
            Q99=makeQuery(id+"F0.imprint","IMPRINT",FACE,{"disambiguationData":[TD([[makeQuery(id+"F0.imprint","IMPRINT",EDGE,{"derivedFrom":sQuery(id+"F0.wireOp",EDGE,"E203.bottom")}),-1.0]])]});
            var Q100;
            {var subQ0=sQuery(id+"F0.wireOp",EDGE,"E232.bottom");var subQ1=sQuery(id+"F0.wireOp",EDGE,"E0.right");var subQ2=makeQuery(id+"F0.imprint","INTERSECT",VERTEX,{"derivedFrom":[subQ1,subQ0]});Q100=makeQuery(id+"F0.imprint","IMPRINT",FACE,{"disambiguationData":[TD([[makeQuery(id+"F0.imprint","IMPRINT",EDGE,{"disambiguationData":[TD([[subQ2,-1.0]])],"derivedFrom":subQ1}),-1.0]])]});}
            var Q101;
            {var subQ0=sQuery(id+"F0.wireOp",EDGE,"E232.bottom");var subQ1=sQuery(id+"F0.wireOp",EDGE,"E0.right");var subQ2=makeQuery(id+"F0.imprint","INTERSECT",VERTEX,{"derivedFrom":[subQ1,subQ0]});Q101=makeQuery(id+"F0.imprint","IMPRINT",FACE,{"disambiguationData":[TD([[makeQuery(id+"F0.imprint","IMPRINT",EDGE,{"disambiguationData":[TD([[subQ2,-1.0]])],"derivedFrom":subQ1}),-1.0]])]});}
            var Q102;
            {var subQ0=sQuery(id+"F0.wireOp",EDGE,"E232.bottom");var subQ1=sQuery(id+"F0.wireOp",EDGE,"E0.right");var subQ2=makeQuery(id+"F0.imprint","INTERSECT",VERTEX,{"derivedFrom":[subQ1,subQ0]});Q102=makeQuery(id+"F0.imprint","IMPRINT",FACE,{"disambiguationData":[TD([[makeQuery(id+"F0.imprint","IMPRINT",EDGE,{"disambiguationData":[TD([[subQ2,-1.0]])],"derivedFrom":subQ1}),-1.0]])]});}
            var Q103;
            {var subQ0=sQuery(id+"F0.wireOp",EDGE,"E87.MirrorCS");Q103=makeQuery(id+"F0.imprint","IMPRINT",FACE,{"disambiguationData":[TD([[makeQuery(id+"F0.imprint","IMPRINT",EDGE,{"derivedFrom":subQ0}),1.0]])]});}
            var Q104;
            {var subQ1=sQuery(id+"F0.wireOp",EDGE,"E94.top");var subQ6=sQuery(id+"F0.wireOp",EDGE,"E94.left");var subQ9=makeQuery(id+"F0.imprint","INTERSECT",VERTEX,{"derivedFrom":[subQ1,subQ6]});Q104=makeQuery(id+"F0.imprint","IMPRINT",FACE,{"disambiguationData":[TD([[makeQuery(id+"F0.imprint","IMPRINT",EDGE,{"disambiguationData":[TD([[subQ9,-1.0]])],"derivedFrom":subQ1}),-1.0]])]});}
            var Q105;
            Q105=makeQuery(id+"F0.imprint","IMPRINT",FACE,{"disambiguationData":[TD([[makeQuery(id+"F0.imprint","IMPRINT",EDGE,{"derivedFrom":sQuery(id+"F0.wireOp",EDGE,"E233.bottom")}),1.0]])]});
            var Q106;
            {var subQ0=sQuery(id+"F0.wireOp",EDGE,"E234");Q106=makeQuery(id+"F0.imprint","IMPRINT",FACE,{"disambiguationData":[TD([[makeQuery(id+"F0.imprint","IMPRINT",EDGE,{"derivedFrom":subQ0}),1.0]])]});}
            var Q107;
            {var subQ0=sQuery(id+"F0.wireOp",EDGE,"E234");Q107=makeQuery(id+"F0.imprint","IMPRINT",FACE,{"disambiguationData":[TD([[makeQuery(id+"F0.imprint","IMPRINT",EDGE,{"derivedFrom":subQ0}),-1.0]])]});}
            var Q108;
            {var subQ0=sQuery(id+"F0.wireOp",EDGE,"E157");var subQ7=sQuery(id+"F0.wireOp",EDGE,"E139.MirrorCS");var subQ12=makeQuery(id+"F0.imprint","INTERSECT",VERTEX,{"derivedFrom":[subQ7,subQ0]});Q108=makeQuery(id+"F0.imprint","IMPRINT",FACE,{"disambiguationData":[TD([[makeQuery(id+"F0.imprint","IMPRINT",EDGE,{"disambiguationData":[TD([[subQ12,-1.0]])],"derivedFrom":subQ7}),-1.0]])]});}
            var Q109;
            {var subQ0=sQuery(id+"F0.wireOp",EDGE,"E241");Q109=makeQuery(id+"F0.imprint","IMPRINT",FACE,{"disambiguationData":[TD([[makeQuery(id+"F0.imprint","IMPRINT",EDGE,{"derivedFrom":subQ0}),1.0]])]});}
            var Q110;
            {var subQ0=sQuery(id+"F0.wireOp",EDGE,"E245");Q110=makeQuery(id+"F0.imprint","IMPRINT",FACE,{"disambiguationData":[TD([[makeQuery(id+"F0.imprint","IMPRINT",EDGE,{"derivedFrom":subQ0}),-1.0]])]});}
            var Q111;
            {var subQ0=sQuery(id+"F0.wireOp",EDGE,"E247");Q111=makeQuery(id+"F0.imprint","IMPRINT",FACE,{"disambiguationData":[TD([[makeQuery(id+"F0.imprint","IMPRINT",EDGE,{"derivedFrom":subQ0}),-1.0]])]});}
            var Q112;
            {var subQ4=sQuery(id+"F0.wireOp",EDGE,"E242");Q112=makeQuery(id+"F0.imprint","IMPRINT",FACE,{"disambiguationData":[TD([[makeQuery(id+"F0.imprint","IMPRINT",EDGE,{"derivedFrom":subQ4}),-1.0]])]});}
            var Q113;
            Q113=makeQuery(id+"F0.imprint","IMPRINT",FACE,{"disambiguationData":[TD([[makeQuery(id+"F0.imprint","IMPRINT",EDGE,{"derivedFrom":sQuery(id+"F0.wireOp",EDGE,"E251.bottom")}),1.0]])]});
            var Q114;
            {var subQ3=sQuery(id+"F0.wireOp",EDGE,"E249.bottom");Q114=makeQuery(id+"F0.imprint","IMPRINT",FACE,{"disambiguationData":[TD([[makeQuery(id+"F0.imprint","IMPRINT",EDGE,{"derivedFrom":subQ3}),1.0]])]});}
            var Q115;
            Q115=makeQuery(id+"F0.imprint","IMPRINT",FACE,{"disambiguationData":[TD([[makeQuery(id+"F0.imprint","IMPRINT",EDGE,{"derivedFrom":sQuery(id+"F0.wireOp",EDGE,"E250.bottom")}),-1.0]])]});
            var Q116;
            {var subQ7=sQuery(id+"F0.wireOp",EDGE,"E249.top");Q116=makeQuery(id+"F0.imprint","IMPRINT",FACE,{"disambiguationData":[TD([[makeQuery(id+"F0.imprint","IMPRINT",EDGE,{"derivedFrom":subQ7}),-1.0]])]});}
            var Q117;
            {var subQ7=sQuery(id+"F0.wireOp",EDGE,"E267");Q117=makeQuery(id+"F0.imprint","IMPRINT",FACE,{"disambiguationData":[TD([[makeQuery(id+"F0.imprint","IMPRINT",EDGE,{"derivedFrom":subQ7}),1.0]])]});}
            var Q118;
            {var subQ0=sQuery(id+"F0.wireOp",EDGE,"E268.MirrorCS");Q118=makeQuery(id+"F0.imprint","IMPRINT",FACE,{"disambiguationData":[TD([[makeQuery(id+"F0.imprint","IMPRINT",EDGE,{"derivedFrom":subQ0}),-1.0]])]});}
            var Q119;
            Q119=makeQuery(id+"F0.imprint","IMPRINT",FACE,{"disambiguationData":[TD([[makeQuery(id+"F0.imprint","IMPRINT",EDGE,{"derivedFrom":sQuery(id+"F0.wireOp",EDGE,"E270.MirrorCS")}),1.0]])]});
            var Q120;
            {var subQ6=sQuery(id+"F0.wireOp",EDGE,"E267");Q120=makeQuery(id+"F0.imprint","IMPRINT",FACE,{"disambiguationData":[TD([[makeQuery(id+"F0.imprint","IMPRINT",EDGE,{"derivedFrom":subQ6}),-1.0]])]});}
            var Q121;
            {var subQ0=sQuery(id+"F0.wireOp",EDGE,"E262");Q121=makeQuery(id+"F0.imprint","IMPRINT",FACE,{"disambiguationData":[TD([[makeQuery(id+"F0.imprint","IMPRINT",EDGE,{"derivedFrom":subQ0}),1.0]])]});}
            var Q122;
            {var subQ0=sQuery(id+"F0.wireOp",EDGE,"E262");Q122=makeQuery(id+"F0.imprint","IMPRINT",FACE,{"disambiguationData":[TD([[makeQuery(id+"F0.imprint","IMPRINT",EDGE,{"derivedFrom":subQ0}),-1.0]])]});}
            var Q123;
            {var subQ1=sQuery(id+"F0.wireOp",EDGE,"E304.right");var subQ7=sQuery(id+"F0.wireOp",EDGE,"E304.bottom");var subQ8=makeQuery(id+"F0.imprint","INTERSECT",VERTEX,{"derivedFrom":[subQ7,subQ1]});Q123=makeQuery(id+"F0.imprint","IMPRINT",FACE,{"disambiguationData":[TD([[makeQuery(id+"F0.imprint","IMPRINT",EDGE,{"disambiguationData":[TD([[subQ8,1.0]])],"derivedFrom":subQ7}),1.0]])]});}
            var Q124;
            {var subQ0=sQuery(id+"F0.wireOp",EDGE,"E309");var subQ1=sQuery(id+"F0.wireOp",EDGE,"E307");var subQ2=makeQuery(id+"F0.imprint","INTERSECT",VERTEX,{"derivedFrom":[subQ1,subQ0]});Q124=makeQuery(id+"F0.imprint","IMPRINT",FACE,{"disambiguationData":[TD([[makeQuery(id+"F0.imprint","IMPRINT",EDGE,{"disambiguationData":[TD([[subQ2,-1.0]])],"derivedFrom":subQ1}),-1.0]])]});}
            var Q125;
            {var subQ1=sQuery(id+"F0.wireOp",EDGE,"E304.left");var subQ5=sQuery(id+"F0.wireOp",EDGE,"E304.bottom");var subQ6=makeQuery(id+"F0.imprint","INTERSECT",VERTEX,{"derivedFrom":[subQ5,subQ1]});Q125=makeQuery(id+"F0.imprint","IMPRINT",FACE,{"disambiguationData":[TD([[makeQuery(id+"F0.imprint","IMPRINT",EDGE,{"disambiguationData":[TD([[subQ6,-1.0]])],"derivedFrom":subQ5}),1.0]])]});}
            var Q126;
            {var subQ1=sQuery(id+"F0.wireOp",EDGE,"E304.right");var subQ5=sQuery(id+"F0.wireOp",EDGE,"E304.top");var subQ6=makeQuery(id+"F0.imprint","INTERSECT",VERTEX,{"derivedFrom":[subQ5,subQ1]});Q126=makeQuery(id+"F0.imprint","IMPRINT",FACE,{"disambiguationData":[TD([[makeQuery(id+"F0.imprint","IMPRINT",EDGE,{"disambiguationData":[TD([[subQ6,1.0]])],"derivedFrom":subQ5}),-1.0]])]});}
            var Q127;
            {var subQ1=sQuery(id+"F0.wireOp",EDGE,"E304.top");var subQ7=sQuery(id+"F0.wireOp",EDGE,"E304.left");var subQ8=makeQuery(id+"F0.imprint","INTERSECT",VERTEX,{"derivedFrom":[subQ1,subQ7]});Q127=makeQuery(id+"F0.imprint","IMPRINT",FACE,{"disambiguationData":[TD([[makeQuery(id+"F0.imprint","IMPRINT",EDGE,{"disambiguationData":[TD([[subQ8,-1.0]])],"derivedFrom":subQ1}),-1.0]])]});}
            var Q128;
            {var subQ0=sQuery(id+"F0.wireOp",EDGE,"E307");var subQ1=sQuery(id+"F0.wireOp",EDGE,"E304.right");var subQ2=makeQuery(id+"F0.imprint","INTERSECT",VERTEX,{"derivedFrom":[subQ1,subQ0]});Q128=makeQuery(id+"F0.imprint","IMPRINT",FACE,{"disambiguationData":[TD([[makeQuery(id+"F0.imprint","IMPRINT",EDGE,{"disambiguationData":[TD([[subQ2,1.0]])],"derivedFrom":subQ1}),1.0]])]});}
            var Q129;
            {var subQ0=sQuery(id+"F0.wireOp",EDGE,"E307");var subQ1=sQuery(id+"F0.wireOp",EDGE,"E304.bottom");var subQ2=makeQuery(id+"F0.imprint","INTERSECT",VERTEX,{"derivedFrom":[subQ1,subQ0]});Q129=makeQuery(id+"F0.imprint","IMPRINT",FACE,{"disambiguationData":[TD([[makeQuery(id+"F0.imprint","IMPRINT",EDGE,{"disambiguationData":[TD([[subQ2,-1.0]])],"derivedFrom":subQ1}),1.0]])]});}
            var Q130;
            {var subQ0=sQuery(id+"F0.wireOp",EDGE,"E308");var subQ1=sQuery(id+"F0.wireOp",EDGE,"E304.top");var subQ2=makeQuery(id+"F0.imprint","INTERSECT",VERTEX,{"derivedFrom":[subQ1,subQ0]});Q130=makeQuery(id+"F0.imprint","IMPRINT",FACE,{"disambiguationData":[TD([[makeQuery(id+"F0.imprint","IMPRINT",EDGE,{"disambiguationData":[TD([[subQ2,1.0]])],"derivedFrom":subQ1}),-1.0]])]});}
            var Q131;
            {var subQ0=sQuery(id+"F0.wireOp",EDGE,"E308");var subQ1=sQuery(id+"F0.wireOp",EDGE,"E304.left");var subQ2=makeQuery(id+"F0.imprint","INTERSECT",VERTEX,{"derivedFrom":[subQ1,subQ0]});Q131=makeQuery(id+"F0.imprint","IMPRINT",FACE,{"disambiguationData":[TD([[makeQuery(id+"F0.imprint","IMPRINT",EDGE,{"disambiguationData":[TD([[subQ2,-1.0]])],"derivedFrom":subQ1}),-1.0]])]});}
            var Q132;
            {var subQ0=sQuery(id+"F0.wireOp",EDGE,"qggExeE8-kWGo-u9pz-UQar-IkqBfX1M3ap2");Q132=makeQuery(id+"F0.imprint","IMPRINT",FACE,{"disambiguationData":[TD([[makeQuery(id+"F0.imprint","IMPRINT",EDGE,{"derivedFrom":subQ0}),-1.0]])]});}
            var Q133;
            {var subQ0=sQuery(id+"F0.wireOp",EDGE,"66b8c4ee-29a5-4347-b911-b6c6981be9150.MirrorCS");Q133=makeQuery(id+"F0.imprint","IMPRINT",FACE,{"disambiguationData":[TD([[makeQuery(id+"F0.imprint","IMPRINT",EDGE,{"derivedFrom":subQ0}),1.0]])]});}
            var Q134;
            {var subQ0=sQuery(id+"F0.wireOp",EDGE,"Ez4gFrAC-GXf4-W1hJ-AaRc-HDuYAol22tyu");Q134=makeQuery(id+"F0.imprint","IMPRINT",FACE,{"disambiguationData":[TD([[makeQuery(id+"F0.imprint","IMPRINT",EDGE,{"derivedFrom":subQ0}),-1.0]])]});}
            var Q135;
            {var subQ0=sQuery(id+"F0.wireOp",EDGE,"9c3ad58d-45c2-4131-8cc4-20bc3f0e06c30.MirrorCS");Q135=makeQuery(id+"F0.imprint","IMPRINT",FACE,{"disambiguationData":[TD([[makeQuery(id+"F0.imprint","IMPRINT",EDGE,{"derivedFrom":subQ0}),1.0]])]});}
            var Q136;
            {var subQ2=sQuery(id+"F0.wireOp",EDGE,"E241");Q136=makeQuery(id+"F0.imprint","IMPRINT",FACE,{"disambiguationData":[TD([[makeQuery(id+"F0.imprint","IMPRINT",EDGE,{"derivedFrom":subQ2}),-1.0]])]});}
            var Q137;
            {var subQ0=sQuery(id+"F0.wireOp",EDGE,"E242");Q137=makeQuery(id+"F0.imprint","IMPRINT",FACE,{"disambiguationData":[TD([[makeQuery(id+"F0.imprint","IMPRINT",EDGE,{"derivedFrom":subQ0}),1.0]])]});}
            var Q138;
            Q138=makeQuery(id+"F0.imprint","IMPRINT",FACE,{"disambiguationData":[TD([[makeQuery(id+"F0.imprint","IMPRINT",EDGE,{"derivedFrom":sQuery(id+"F0.wireOp",EDGE,"E231.bottom")}),-1.0]])]});
            extrude(context, id + "F1", {"entities" : qUnion([Q0, Q1, Q2, Q3, Q4, Q5, Q6, Q7, Q8, Q9, Q10, Q11, Q12, Q13, Q14, Q15, Q16, Q17, Q18, Q19, Q20, Q21, Q22, Q23, Q24, Q25, Q26, Q27, Q28, Q29, Q30, Q31, Q32, Q33, Q34, Q35, Q36, Q37, Q38, Q39, Q40, Q41, Q42, Q43, Q44, Q45, Q46, Q47, Q48, Q49, Q50, Q51, Q52, Q53, Q54, Q55, Q56, Q57, Q58, Q59, Q60, Q61, Q62, Q63, Q64, Q65, Q66, Q67, Q68, Q69, Q70, Q71, Q72, Q73, Q74, Q75, Q76, Q77, Q78, Q79, Q80, Q81, Q82, Q83, Q84, Q85, Q86, Q87, Q88, Q89, Q90, Q91, Q92, Q93, Q94, Q95, Q96, Q97, Q98, Q99, Q100, Q101, Q102, Q103, Q104, Q105, Q106, Q107, Q108, Q109, Q110, Q111, Q112, Q113, Q114, Q115, Q116, Q117, Q118, Q119, Q120, Q121, Q122, Q123, Q124, Q125, Q126, Q127, Q128, Q129, Q130, Q131, Q132, Q133, Q134, Q135, Q136, Q137, Q138]), "depth" : 3.17 * mm});
        }
        {
            var Q0;
            {var subQ0=sQuery(id+"F0.wireOp",EDGE,"E129.right");Q0=makeQuery(id+"F0.imprint","IMPRINT",FACE,{"disambiguationData":[TD([[makeQuery(id+"F0.imprint","IMPRINT",EDGE,{"derivedFrom":subQ0}),1.0]])]});}
            var Q1;
            {var subQ1=sQuery(id+"F0.wireOp",EDGE,"E129.left");Q1=makeQuery(id+"F0.imprint","IMPRINT",FACE,{"disambiguationData":[TD([[makeQuery(id+"F0.imprint","IMPRINT",EDGE,{"derivedFrom":subQ1}),-1.0]])]});}
            extrude(context, id + "F2", {"entities" : qUnion([Q0, Q1]), "depth" : 7 * mm});
        }
        {
            var Q0;
            Q0=makeQuery(id+"F2.opExtrude","SWEPT_FACE",FACE,{"disambiguationData":[OSD([sQuery(id+"F0.wireOp",EDGE,"E129.bottom")])]});
            var sketch = newSketch(context, id + "F3", { "sketchPlane" : qUnion([Q0])});
            skLineSegment(sketch, "E313.bottom", {"start": v(96.08, 0) * mm, "end": v(61.08, 0) * mm});
            skLineSegment(sketch, "E313.top", {"start": v(96.08, 50) * mm, "end": v(61.08, 50) * mm});
            skLineSegment(sketch, "E313.left", {"start": v(96.08, 0) * mm, "end": v(96.08, 50) * mm});
            skLineSegment(sketch, "E313.right", {"start": v(61.08, 0) * mm, "end": v(61.08, 50) * mm});
            skSolve(sketch);
        }
        {
            var Q0;
            {var subQ0=sQuery(id+"F3.wireOp",EDGE,"E313.top");Q0=makeQuery(id+"F3.imprint","IMPRINT",FACE,{"disambiguationData":[TD([[makeQuery(id+"F3.imprint","IMPRINT",EDGE,{"derivedFrom":subQ0}),1.0]])]});}
            var Q1;
            {var subQ0=sQuery(id+"F3.wireOp",EDGE,"E313.bottom");Q1=makeQuery(id+"F3.imprint","IMPRINT",FACE,{"disambiguationData":[TD([[makeQuery(id+"F3.imprint","IMPRINT",EDGE,{"derivedFrom":subQ0}),1.0]])]});}
            extrude(context, id + "F4", {"entities" : qUnion([Q0, Q1]), "operationType" : NewBodyOperationType.ADD, "depth" : 7 * mm});
        }
        {
            var Q0;
            Q0=makeQuery(id+"F2.opExtrude","CAP_EDGE",EDGE,{"disambiguationData":[OSD([sQuery(id+"F0.wireOp",EDGE,"E129.bottom")])],"isStart":false});
            var Q1;
            Q1=makeQuery(id+"F2.opExtrude","SWEPT_EDGE",EDGE,{"disambiguationData":[OSD([sQuery(id+"F0.wireOp",EDGE,"E129.top"),sQuery(id+"F0.wireOp",EDGE,"E129.left")])]});
            var Q2;
            Q2=makeQuery(id+"F2.opExtrude","SWEPT_EDGE",EDGE,{"disambiguationData":[OSD([sQuery(id+"F0.wireOp",EDGE,"E129.top"),sQuery(id+"F0.wireOp",EDGE,"E129.right")])]});
            var Q3;
            Q3=makeQuery(id+"F4.opExtrude","SWEPT_EDGE",EDGE,{"disambiguationData":[OSD([sQuery(id+"F3.wireOp",EDGE,"E313.top"),sQuery(id+"F3.wireOp",EDGE,"E313.right")])]});
            var Q4;
            Q4=makeQuery(id+"F4.opExtrude","SWEPT_EDGE",EDGE,{"disambiguationData":[OSD([sQuery(id+"F3.wireOp",EDGE,"E313.top"),sQuery(id+"F3.wireOp",EDGE,"E313.left")])]});
            var Q5;
            Q5=makeQuery(id+"F4.opExtrude","CAP_EDGE",EDGE,{"disambiguationData":[OSD([sQuery(id+"F3.wireOp",EDGE,"E313.bottom")])],"isStart":false});
            fillet(context, id + "F5", {"entities" : qUnion([Q0, Q1, Q2, Q3, Q4, Q5]), "radius" : 5 * mm, "tangentPropagation" : true, "allowEdgeOverflow" : false});
        }
        {
            var Q0;
            Q0=makeQuery(id+"F4.opExtrude","CAP_FACE",FACE,{"disambiguationData":[OSD([sQuery(id+"F3.wireOp",EDGE,"E313.bottom"),sQuery(id+"F3.wireOp",EDGE,"E313.top"),sQuery(id+"F3.wireOp",EDGE,"E313.left"),sQuery(id+"F3.wireOp",EDGE,"E313.right")])],"isStart":false});
            var sketch = newSketch(context, id + "F6", { "sketchPlane" : qUnion([Q0])});
            skCircle(sketch, "E314", {"center": v(69.83, 43.5) * mm, "radius": 1.5 * mm});
            skLineSegment(sketch, "E315", {"start": v(78.58, 50) * mm, "end": v(78.58, 5) * mm});
            skCircle(sketch, "E316.MirrorC", {"center": v(87.33, 43.5) * mm, "radius": 1.5 * mm});
            skSolve(sketch);
        }
        {
            var Q0;
            Q0=makeQuery(id+"F6.imprint","IMPRINT",FACE,{"disambiguationData":[TD([[makeQuery(id+"F6.imprint","IMPRINT",EDGE,{"derivedFrom":sQuery(id+"F6.wireOp",EDGE,"E314")}),1.0]])]});
            var Q1;
            Q1=makeQuery(id+"F6.imprint","IMPRINT",FACE,{"disambiguationData":[TD([[makeQuery(id+"F6.imprint","IMPRINT",EDGE,{"derivedFrom":sQuery(id+"F6.wireOp",EDGE,"08264b1d-ac39-41e3-a3a1-aa4644afc9580.MirrorC")}),-1.0]])]});
            var Q2;
            Q2=makeQuery(id+"F6.imprint","IMPRINT",FACE,{"disambiguationData":[TD([[makeQuery(id+"F6.imprint","IMPRINT",EDGE,{"derivedFrom":sQuery(id+"F6.wireOp",EDGE,"E316.MirrorC")}),-1.0]])]});
            extrude(context, id + "F7", {"entities" : qUnion([Q0, Q1, Q2]), "operationType" : NewBodyOperationType.REMOVE, "oppositeDirection" : true, "depth" : 7 * mm});
        }
        {
            var Q0;
            Q0=makeQuery(id+"F0.imprint","IMPRINT",FACE,{"disambiguationData":[TD([[makeQuery(id+"F0.imprint","IMPRINT",EDGE,{"derivedFrom":sQuery(id+"F0.wireOp",EDGE,"E164")}),1.0]])]});
            extrude(context, id + "F8", {"entities" : qUnion([Q0]), "depth" : 94.44 * mm});
        }
        {
            var Q0;
            Q0=makeQuery(id+"F1.opExtrude","SWEPT_EDGE",EDGE,{"disambiguationData":[OSD([sQuery(id+"F0.wireOp",EDGE,"E233.bottom"),sQuery(id+"F0.wireOp",EDGE,"E233.left")])]});
            var Q1;
            Q1=makeQuery(id+"F1.opExtrude","SWEPT_EDGE",EDGE,{"disambiguationData":[OSD([sQuery(id+"F0.wireOp",EDGE,"E233.bottom"),sQuery(id+"F0.wireOp",EDGE,"E233.right")])]});
            fillet(context, id + "F9", {"entities" : qUnion([Q0, Q1]), "radius" : 5 * mm, "tangentPropagation" : true, "allowEdgeOverflow" : false});
        }
        {
            var Q0;
            Q0=makeQuery(id+"F1.opExtrude","SWEPT_EDGE",EDGE,{"disambiguationData":[OSD([sQuery(id+"F0.wireOp",EDGE,"E241"),sQuery(id+"F0.wireOp",EDGE,"E311")])]});
            var Q1;
            Q1=makeQuery(id+"F1.opExtrude","SWEPT_EDGE",EDGE,{"disambiguationData":[OSD([sQuery(id+"F0.wireOp",EDGE,"E157"),sQuery(id+"F0.wireOp",EDGE,"E311")])]});
            var Q2;
            Q2=makeQuery(id+"F1.opExtrude","SWEPT_EDGE",EDGE,{"disambiguationData":[OSD([sQuery(id+"F0.wireOp",EDGE,"E242"),sQuery(id+"F0.wireOp",EDGE,"E312.MirrorCS")])]});
            var Q3;
            Q3=makeQuery(id+"F1.opExtrude","SWEPT_EDGE",EDGE,{"disambiguationData":[OSD([sQuery(id+"F0.wireOp",EDGE,"E157"),sQuery(id+"F0.wireOp",EDGE,"E312.MirrorCS")])]});
            fillet(context, id + "F10", {"entities" : qUnion([Q0, Q1, Q2, Q3]), "radius" : 5 * mm, "tangentPropagation" : true, "allowEdgeOverflow" : false});
        }
    });
